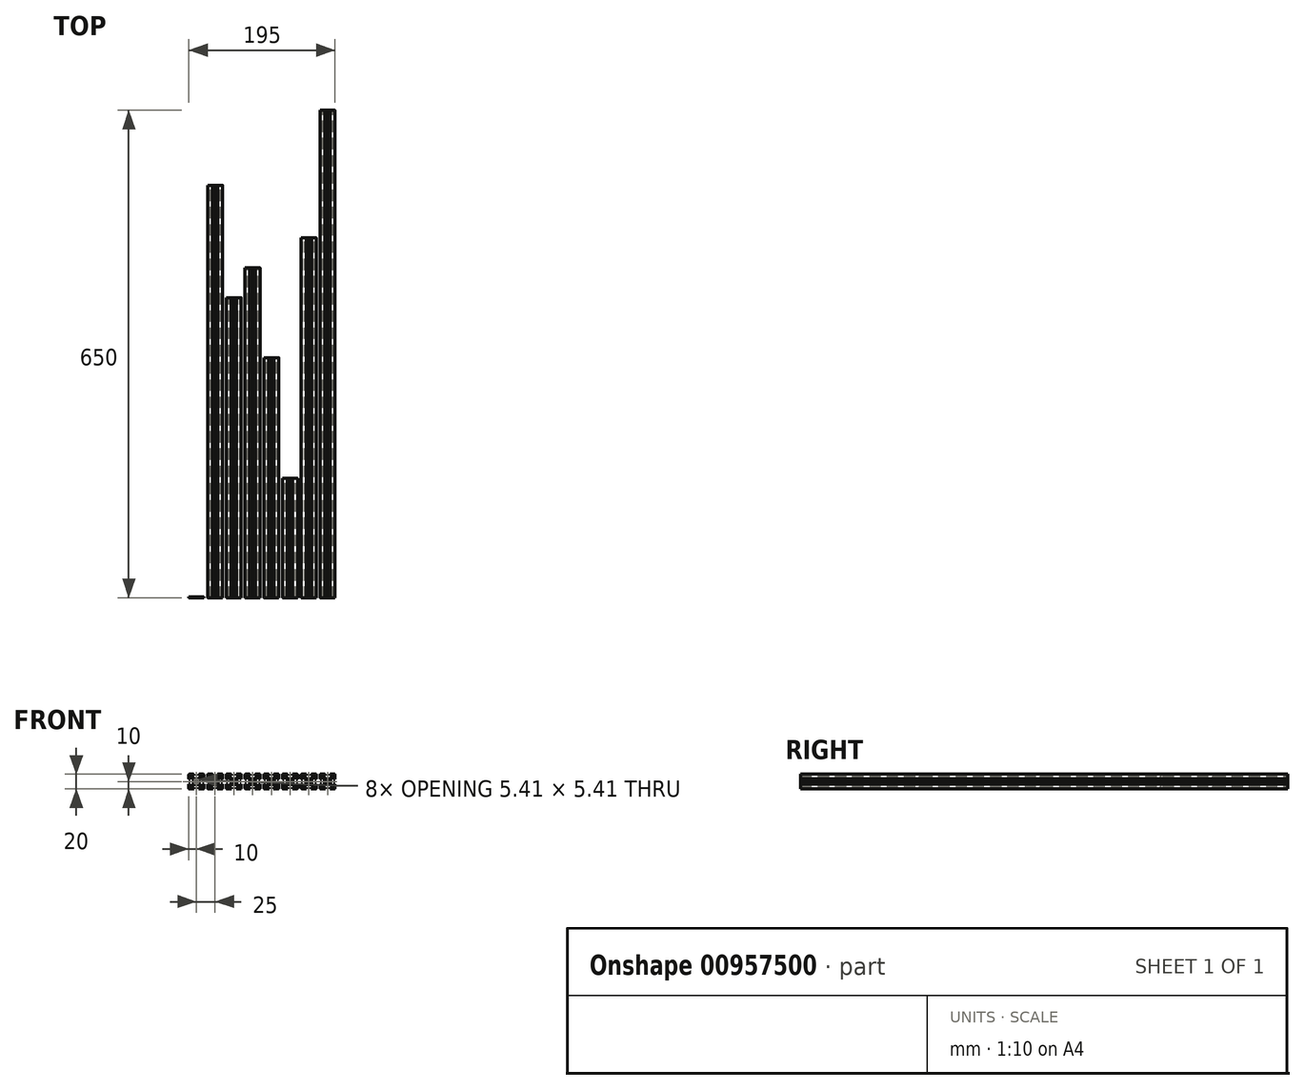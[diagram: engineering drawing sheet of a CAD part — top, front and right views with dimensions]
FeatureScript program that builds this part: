
annotation { "Feature Type Name" : "Feature", "Feature Type Description" : "" }
export const myFeature = defineFeature(function(context is Context, id is Id, definition is map)
    precondition{}
    {
        {
            var Q0;
            Q0=qCreatedBy(makeId("Front.planeOp"),FACE);
            var sketch = newSketch(context, id + "F0", { "sketchPlane" : qUnion([Q0])});
            skArc(sketch, "E0", {"start": v(3.9, -2.93) * mm, "mid": v(3.92, -3.04) * mm, "end": v(3.99, -3.14) * mm});
            skLineSegment(sketch, "E1", {"start": v(3.9, -0.5) * mm, "end": v(3.9, -2.93) * mm});
            skLineSegment(sketch, "E2", {"start": v(3.61, -0.21) * mm, "end": v(3.9, -0.5) * mm});
            skArc(sketch, "E3", {"start": v(3.61, 0.21) * mm, "mid": v(3.52, 0) * mm, "end": v(3.61, -0.21) * mm});
            skLineSegment(sketch, "E4", {"start": v(3.61, 0.21) * mm, "end": v(3.9, 0.5) * mm});
            skLineSegment(sketch, "E5", {"start": v(3.9, 2.93) * mm, "end": v(3.9, 0.5) * mm});
            skArc(sketch, "E6", {"start": v(3.99, 3.14) * mm, "mid": v(3.92, 3.04) * mm, "end": v(3.9, 2.93) * mm});
            skLineSegment(sketch, "E7", {"start": v(3.99, 3.14) * mm, "end": v(6.26, 5.41) * mm});
            skArc(sketch, "E8", {"start": v(6.47, 5.5) * mm, "mid": v(6.36, 5.48) * mm, "end": v(6.26, 5.41) * mm});
            skLineSegment(sketch, "E9", {"start": v(6.47, 5.5) * mm, "end": v(8.1, 5.5) * mm});
            skLineSegment(sketch, "E10", {"start": v(8.1, 3.1) * mm, "end": v(8.1, 5.5) * mm});
            skLineSegment(sketch, "E11", {"start": v(9.5, 3.1) * mm, "end": v(8.1, 3.1) * mm});
            skLineSegment(sketch, "E12", {"start": v(9.5, 3.6) * mm, "end": v(9.5, 3.1) * mm});
            skLineSegment(sketch, "E13", {"start": v(10, 3.6) * mm, "end": v(9.5, 3.6) * mm});
            skLineSegment(sketch, "E14", {"start": v(10, 9) * mm, "end": v(10, 3.6) * mm});
            skArc(sketch, "E15", {"start": v(10, 9) * mm, "mid": v(9.7, 9.7) * mm, "end": v(9, 10) * mm});
            skLineSegment(sketch, "E16", {"start": v(9, 10) * mm, "end": v(3.6, 10) * mm});
            skLineSegment(sketch, "E17", {"start": v(3.6, 9.5) * mm, "end": v(3.6, 10) * mm});
            skLineSegment(sketch, "E18", {"start": v(3.1, 9.5) * mm, "end": v(3.6, 9.5) * mm});
            skLineSegment(sketch, "E19", {"start": v(3.1, 9.5) * mm, "end": v(3.1, 8.1) * mm});
            skLineSegment(sketch, "E20", {"start": v(3.1, 8.1) * mm, "end": v(5.5, 8.1) * mm});
            skLineSegment(sketch, "E21", {"start": v(5.5, 8.1) * mm, "end": v(5.5, 6.47) * mm});
            skArc(sketch, "E22", {"start": v(5.41, 6.26) * mm, "mid": v(5.48, 6.36) * mm, "end": v(5.5, 6.47) * mm});
            skLineSegment(sketch, "E23", {"start": v(3.14, 3.99) * mm, "end": v(5.41, 6.26) * mm});
            skArc(sketch, "E24", {"start": v(2.93, 3.9) * mm, "mid": v(3.04, 3.92) * mm, "end": v(3.14, 3.99) * mm});
            skLineSegment(sketch, "E25", {"start": v(0.5, 3.9) * mm, "end": v(2.93, 3.9) * mm});
            skLineSegment(sketch, "E26", {"start": v(0.21, 3.61) * mm, "end": v(0.5, 3.9) * mm});
            skArc(sketch, "E27", {"start": v(-0.21, 3.61) * mm, "mid": v(0, 3.52) * mm, "end": v(0.21, 3.61) * mm});
            skLineSegment(sketch, "E28", {"start": v(-0.21, 3.61) * mm, "end": v(-0.5, 3.9) * mm});
            skLineSegment(sketch, "E29", {"start": v(-2.93, 3.9) * mm, "end": v(-0.5, 3.9) * mm});
            skArc(sketch, "E30", {"start": v(-3.14, 3.99) * mm, "mid": v(-3.04, 3.92) * mm, "end": v(-2.93, 3.9) * mm});
            skLineSegment(sketch, "E31", {"start": v(-5.41, 6.26) * mm, "end": v(-3.14, 3.99) * mm});
            skArc(sketch, "E32", {"start": v(-5.5, 6.47) * mm, "mid": v(-5.48, 6.36) * mm, "end": v(-5.41, 6.26) * mm});
            skLineSegment(sketch, "E33", {"start": v(-5.5, 6.47) * mm, "end": v(-5.5, 8.1) * mm});
            skLineSegment(sketch, "E34", {"start": v(-3.1, 8.1) * mm, "end": v(-5.5, 8.1) * mm});
            skLineSegment(sketch, "E35", {"start": v(-3.1, 9.5) * mm, "end": v(-3.1, 8.1) * mm});
            skLineSegment(sketch, "E36", {"start": v(-3.1, 9.5) * mm, "end": v(-3.6, 9.5) * mm});
            skLineSegment(sketch, "E37", {"start": v(-3.6, 9.5) * mm, "end": v(-3.6, 10) * mm});
            skLineSegment(sketch, "E38", {"start": v(-9, 10) * mm, "end": v(-3.6, 10) * mm});
            skArc(sketch, "E39", {"start": v(-9, 10) * mm, "mid": v(-9.7, 9.7) * mm, "end": v(-10, 9) * mm});
            skLineSegment(sketch, "E40", {"start": v(-10, 9) * mm, "end": v(-10, 3.6) * mm});
            skLineSegment(sketch, "E41", {"start": v(-10, 3.6) * mm, "end": v(-9.5, 3.6) * mm});
            skLineSegment(sketch, "E42", {"start": v(-9.5, 3.6) * mm, "end": v(-9.5, 3.1) * mm});
            skLineSegment(sketch, "E43", {"start": v(-9.5, 3.1) * mm, "end": v(-8.1, 3.1) * mm});
            skLineSegment(sketch, "E44", {"start": v(-8.1, 3.1) * mm, "end": v(-8.1, 5.5) * mm});
            skLineSegment(sketch, "E45", {"start": v(-8.1, 5.5) * mm, "end": v(-6.47, 5.5) * mm});
            skArc(sketch, "E46", {"start": v(-6.26, 5.41) * mm, "mid": v(-6.36, 5.48) * mm, "end": v(-6.47, 5.5) * mm});
            skLineSegment(sketch, "E47", {"start": v(-3.99, 3.14) * mm, "end": v(-6.26, 5.41) * mm});
            skArc(sketch, "E48", {"start": v(-3.9, 2.93) * mm, "mid": v(-3.92, 3.04) * mm, "end": v(-3.99, 3.14) * mm});
            skLineSegment(sketch, "E49", {"start": v(-3.9, 2.93) * mm, "end": v(-3.9, 0.5) * mm});
            skLineSegment(sketch, "E50", {"start": v(-3.61, 0.21) * mm, "end": v(-3.9, 0.5) * mm});
            skArc(sketch, "E51", {"start": v(-3.61, -0.21) * mm, "mid": v(-3.52, 0) * mm, "end": v(-3.61, 0.21) * mm});
            skLineSegment(sketch, "E52", {"start": v(-3.61, -0.21) * mm, "end": v(-3.9, -0.5) * mm});
            skLineSegment(sketch, "E53", {"start": v(-3.9, -0.5) * mm, "end": v(-3.9, -2.93) * mm});
            skArc(sketch, "E54", {"start": v(-3.99, -3.14) * mm, "mid": v(-3.92, -3.04) * mm, "end": v(-3.9, -2.93) * mm});
            skLineSegment(sketch, "E55", {"start": v(-6.26, -5.41) * mm, "end": v(-3.99, -3.14) * mm});
            skArc(sketch, "E56", {"start": v(-6.47, -5.5) * mm, "mid": v(-6.36, -5.48) * mm, "end": v(-6.26, -5.41) * mm});
            skLineSegment(sketch, "E57", {"start": v(-6.47, -5.5) * mm, "end": v(-8.1, -5.5) * mm});
            skLineSegment(sketch, "E58", {"start": v(-8.1, -3.1) * mm, "end": v(-8.1, -5.5) * mm});
            skLineSegment(sketch, "E59", {"start": v(-9.5, -3.1) * mm, "end": v(-8.1, -3.1) * mm});
            skLineSegment(sketch, "E60", {"start": v(-9.5, -3.6) * mm, "end": v(-9.5, -3.1) * mm});
            skLineSegment(sketch, "E61", {"start": v(-10, -3.6) * mm, "end": v(-9.5, -3.6) * mm});
            skLineSegment(sketch, "E62", {"start": v(-10, -3.6) * mm, "end": v(-10, -9) * mm});
            skArc(sketch, "E63", {"start": v(-10, -9) * mm, "mid": v(-9.7, -9.7) * mm, "end": v(-9, -10) * mm});
            skLineSegment(sketch, "E64", {"start": v(-9, -10) * mm, "end": v(-3.6, -10) * mm});
            skLineSegment(sketch, "E65", {"start": v(-3.6, -9.5) * mm, "end": v(-3.6, -10) * mm});
            skLineSegment(sketch, "E66", {"start": v(-3.1, -9.5) * mm, "end": v(-3.6, -9.5) * mm});
            skLineSegment(sketch, "E67", {"start": v(-3.1, -9.5) * mm, "end": v(-3.1, -8.1) * mm});
            skLineSegment(sketch, "E68", {"start": v(-3.1, -8.1) * mm, "end": v(-5.5, -8.1) * mm});
            skLineSegment(sketch, "E69", {"start": v(-5.5, -8.1) * mm, "end": v(-5.5, -6.47) * mm});
            skArc(sketch, "E70", {"start": v(-5.41, -6.26) * mm, "mid": v(-5.48, -6.36) * mm, "end": v(-5.5, -6.47) * mm});
            skLineSegment(sketch, "E71", {"start": v(-3.14, -3.99) * mm, "end": v(-5.41, -6.26) * mm});
            skArc(sketch, "E72", {"start": v(-2.93, -3.9) * mm, "mid": v(-3.04, -3.92) * mm, "end": v(-3.14, -3.99) * mm});
            skLineSegment(sketch, "E73", {"start": v(-2.93, -3.9) * mm, "end": v(-0.5, -3.9) * mm});
            skLineSegment(sketch, "E74", {"start": v(-0.21, -3.61) * mm, "end": v(-0.5, -3.9) * mm});
            skArc(sketch, "E75", {"start": v(0.21, -3.61) * mm, "mid": v(0, -3.52) * mm, "end": v(-0.21, -3.61) * mm});
            skLineSegment(sketch, "E76", {"start": v(0.21, -3.61) * mm, "end": v(0.5, -3.9) * mm});
            skLineSegment(sketch, "E77", {"start": v(0.5, -3.9) * mm, "end": v(2.93, -3.9) * mm});
            skArc(sketch, "E78", {"start": v(3.14, -3.99) * mm, "mid": v(3.04, -3.92) * mm, "end": v(2.93, -3.9) * mm});
            skLineSegment(sketch, "E79", {"start": v(5.41, -6.26) * mm, "end": v(3.14, -3.99) * mm});
            skArc(sketch, "E80", {"start": v(5.5, -6.47) * mm, "mid": v(5.48, -6.36) * mm, "end": v(5.41, -6.26) * mm});
            skLineSegment(sketch, "E81", {"start": v(5.5, -8.1) * mm, "end": v(5.5, -6.47) * mm});
            skLineSegment(sketch, "E82", {"start": v(3.1, -8.1) * mm, "end": v(5.5, -8.1) * mm});
            skLineSegment(sketch, "E83", {"start": v(3.1, -9.5) * mm, "end": v(3.1, -8.1) * mm});
            skLineSegment(sketch, "E84", {"start": v(3.1, -9.5) * mm, "end": v(3.6, -9.5) * mm});
            skLineSegment(sketch, "E85", {"start": v(3.6, -9.5) * mm, "end": v(3.6, -10) * mm});
            skLineSegment(sketch, "E86", {"start": v(3.6, -10) * mm, "end": v(9, -10) * mm});
            skArc(sketch, "E87", {"start": v(9, -10) * mm, "mid": v(9.7, -9.7) * mm, "end": v(10, -9) * mm});
            skLineSegment(sketch, "E88", {"start": v(10, -3.6) * mm, "end": v(10, -9) * mm});
            skLineSegment(sketch, "E89", {"start": v(10, -3.6) * mm, "end": v(9.5, -3.6) * mm});
            skLineSegment(sketch, "E90", {"start": v(9.5, -3.6) * mm, "end": v(9.5, -3.1) * mm});
            skLineSegment(sketch, "E91", {"start": v(9.5, -3.1) * mm, "end": v(8.1, -3.1) * mm});
            skLineSegment(sketch, "E92", {"start": v(8.1, -3.1) * mm, "end": v(8.1, -5.5) * mm});
            skLineSegment(sketch, "E93", {"start": v(6.47, -5.5) * mm, "end": v(8.1, -5.5) * mm});
            skArc(sketch, "E94", {"start": v(6.26, -5.41) * mm, "mid": v(6.36, -5.48) * mm, "end": v(6.47, -5.5) * mm});
            skLineSegment(sketch, "E95", {"start": v(3.99, -3.14) * mm, "end": v(6.26, -5.41) * mm});
            skLineSegment(sketch, "E96", {"start": v(-1.9, 2.62) * mm, "end": v(-1.54, 2.25) * mm});
            skArc(sketch, "E97", {"start": v(-1.54, 2.25) * mm, "mid": v(-1.37, 2.17) * mm, "end": v(-1.19, 2.2) * mm});
            skArc(sketch, "E98", {"start": v(1.19, 2.2) * mm, "mid": v(0, 2.5) * mm, "end": v(-1.19, 2.2) * mm});
            skArc(sketch, "E99", {"start": v(1.19, 2.2) * mm, "mid": v(1.37, 2.17) * mm, "end": v(1.54, 2.25) * mm});
            skLineSegment(sketch, "E100", {"start": v(1.9, 2.62) * mm, "end": v(1.54, 2.25) * mm});
            skArc(sketch, "E101", {"start": v(2.33, 2.62) * mm, "mid": v(2.12, 2.7) * mm, "end": v(1.9, 2.62) * mm});
            skLineSegment(sketch, "E102", {"start": v(2.62, 2.33) * mm, "end": v(2.33, 2.62) * mm});
            skArc(sketch, "E103", {"start": v(2.62, 1.9) * mm, "mid": v(2.7, 2.12) * mm, "end": v(2.62, 2.33) * mm});
            skLineSegment(sketch, "E104", {"start": v(2.62, 1.9) * mm, "end": v(2.25, 1.54) * mm});
            skArc(sketch, "E105", {"start": v(2.25, 1.54) * mm, "mid": v(2.17, 1.37) * mm, "end": v(2.2, 1.19) * mm});
            skArc(sketch, "E106", {"start": v(2.2, -1.19) * mm, "mid": v(2.5, 0) * mm, "end": v(2.2, 1.19) * mm});
            skArc(sketch, "E107", {"start": v(2.2, -1.19) * mm, "mid": v(2.17, -1.37) * mm, "end": v(2.25, -1.54) * mm});
            skLineSegment(sketch, "E108", {"start": v(2.25, -1.54) * mm, "end": v(2.62, -1.9) * mm});
            skArc(sketch, "E109", {"start": v(2.62, -2.33) * mm, "mid": v(2.7, -2.12) * mm, "end": v(2.62, -1.9) * mm});
            skLineSegment(sketch, "E110", {"start": v(2.33, -2.62) * mm, "end": v(2.62, -2.33) * mm});
            skArc(sketch, "E111", {"start": v(1.9, -2.62) * mm, "mid": v(2.12, -2.7) * mm, "end": v(2.33, -2.62) * mm});
            skLineSegment(sketch, "E112", {"start": v(1.54, -2.25) * mm, "end": v(1.9, -2.62) * mm});
            skArc(sketch, "E113", {"start": v(1.54, -2.25) * mm, "mid": v(1.37, -2.17) * mm, "end": v(1.19, -2.2) * mm});
            skArc(sketch, "E114", {"start": v(-1.19, -2.2) * mm, "mid": v(0, -2.5) * mm, "end": v(1.19, -2.2) * mm});
            skArc(sketch, "E115", {"start": v(-1.19, -2.2) * mm, "mid": v(-1.37, -2.17) * mm, "end": v(-1.54, -2.25) * mm});
            skLineSegment(sketch, "E116", {"start": v(-1.54, -2.25) * mm, "end": v(-1.9, -2.62) * mm});
            skArc(sketch, "E117", {"start": v(-2.33, -2.62) * mm, "mid": v(-2.12, -2.7) * mm, "end": v(-1.9, -2.62) * mm});
            skLineSegment(sketch, "E118", {"start": v(-2.62, -2.33) * mm, "end": v(-2.33, -2.62) * mm});
            skArc(sketch, "E119", {"start": v(-2.62, -1.9) * mm, "mid": v(-2.7, -2.12) * mm, "end": v(-2.62, -2.33) * mm});
            skLineSegment(sketch, "E120", {"start": v(-2.25, -1.54) * mm, "end": v(-2.62, -1.9) * mm});
            skArc(sketch, "E121", {"start": v(-2.25, -1.54) * mm, "mid": v(-2.17, -1.37) * mm, "end": v(-2.2, -1.19) * mm});
            skArc(sketch, "E122", {"start": v(-2.2, 1.19) * mm, "mid": v(-2.5, 0) * mm, "end": v(-2.2, -1.19) * mm});
            skArc(sketch, "E123", {"start": v(-2.2, 1.19) * mm, "mid": v(-2.17, 1.37) * mm, "end": v(-2.25, 1.54) * mm});
            skLineSegment(sketch, "E124", {"start": v(-2.62, 1.9) * mm, "end": v(-2.25, 1.54) * mm});
            skArc(sketch, "E125", {"start": v(-2.62, 2.33) * mm, "mid": v(-2.7, 2.12) * mm, "end": v(-2.62, 1.9) * mm});
            skLineSegment(sketch, "E126", {"start": v(-2.33, 2.62) * mm, "end": v(-2.62, 2.33) * mm});
            skArc(sketch, "E127", {"start": v(-1.9, 2.62) * mm, "mid": v(-2.12, 2.7) * mm, "end": v(-2.33, 2.62) * mm});
            skSolve(sketch);
        }
        {
            var Q0;
            Q0=makeQuery(id+"F0.imprint","IMPRINT",FACE,{"disambiguationData":[TD([[makeQuery(id+"F0.imprint","IMPRINT",EDGE,{"derivedFrom":sQuery(id+"F0.wireOp",EDGE,"E0")}),-1.0]])]});
            extrude(context, id + "F1", {"entities" : qUnion([Q0]), "depth" : 1 * mm, "offsetDistance" : 25 * mm});
        }
        {
            var Q0;
            Q0=makeQuery(id+"F1.opExtrude","SWEPT_BODY",BODY,{"disambiguationData":[OSD([sQuery(id+"F0.wireOp",EDGE,"E0"),sQuery(id+"F0.wireOp",EDGE,"E1"),sQuery(id+"F0.wireOp",EDGE,"E2"),sQuery(id+"F0.wireOp",EDGE,"E3"),sQuery(id+"F0.wireOp",EDGE,"E4"),sQuery(id+"F0.wireOp",EDGE,"E5"),sQuery(id+"F0.wireOp",EDGE,"E6"),sQuery(id+"F0.wireOp",EDGE,"E7"),sQuery(id+"F0.wireOp",EDGE,"E8"),sQuery(id+"F0.wireOp",EDGE,"E9"),sQuery(id+"F0.wireOp",EDGE,"E10"),sQuery(id+"F0.wireOp",EDGE,"E11"),sQuery(id+"F0.wireOp",EDGE,"E12"),sQuery(id+"F0.wireOp",EDGE,"E13"),sQuery(id+"F0.wireOp",EDGE,"E14"),sQuery(id+"F0.wireOp",EDGE,"E15"),sQuery(id+"F0.wireOp",EDGE,"E16"),sQuery(id+"F0.wireOp",EDGE,"E17"),sQuery(id+"F0.wireOp",EDGE,"E18"),sQuery(id+"F0.wireOp",EDGE,"E19"),sQuery(id+"F0.wireOp",EDGE,"E20"),sQuery(id+"F0.wireOp",EDGE,"E21"),sQuery(id+"F0.wireOp",EDGE,"E22"),sQuery(id+"F0.wireOp",EDGE,"E23"),sQuery(id+"F0.wireOp",EDGE,"E24"),sQuery(id+"F0.wireOp",EDGE,"E25"),sQuery(id+"F0.wireOp",EDGE,"E26"),sQuery(id+"F0.wireOp",EDGE,"E27"),sQuery(id+"F0.wireOp",EDGE,"E28"),sQuery(id+"F0.wireOp",EDGE,"E29"),sQuery(id+"F0.wireOp",EDGE,"E30"),sQuery(id+"F0.wireOp",EDGE,"E31"),sQuery(id+"F0.wireOp",EDGE,"E32"),sQuery(id+"F0.wireOp",EDGE,"E33"),sQuery(id+"F0.wireOp",EDGE,"E34"),sQuery(id+"F0.wireOp",EDGE,"E35"),sQuery(id+"F0.wireOp",EDGE,"E36"),sQuery(id+"F0.wireOp",EDGE,"E37"),sQuery(id+"F0.wireOp",EDGE,"E38"),sQuery(id+"F0.wireOp",EDGE,"E39"),sQuery(id+"F0.wireOp",EDGE,"E40"),sQuery(id+"F0.wireOp",EDGE,"E41"),sQuery(id+"F0.wireOp",EDGE,"E42"),sQuery(id+"F0.wireOp",EDGE,"E43"),sQuery(id+"F0.wireOp",EDGE,"E44"),sQuery(id+"F0.wireOp",EDGE,"E45"),sQuery(id+"F0.wireOp",EDGE,"E46"),sQuery(id+"F0.wireOp",EDGE,"E47"),sQuery(id+"F0.wireOp",EDGE,"E48"),sQuery(id+"F0.wireOp",EDGE,"E49"),sQuery(id+"F0.wireOp",EDGE,"E50"),sQuery(id+"F0.wireOp",EDGE,"E51"),sQuery(id+"F0.wireOp",EDGE,"E52"),sQuery(id+"F0.wireOp",EDGE,"E53"),sQuery(id+"F0.wireOp",EDGE,"E54"),sQuery(id+"F0.wireOp",EDGE,"E55"),sQuery(id+"F0.wireOp",EDGE,"E56"),sQuery(id+"F0.wireOp",EDGE,"E57"),sQuery(id+"F0.wireOp",EDGE,"E58"),sQuery(id+"F0.wireOp",EDGE,"E59"),sQuery(id+"F0.wireOp",EDGE,"E60"),sQuery(id+"F0.wireOp",EDGE,"E61"),sQuery(id+"F0.wireOp",EDGE,"E62"),sQuery(id+"F0.wireOp",EDGE,"E63"),sQuery(id+"F0.wireOp",EDGE,"E64"),sQuery(id+"F0.wireOp",EDGE,"E65"),sQuery(id+"F0.wireOp",EDGE,"E66"),sQuery(id+"F0.wireOp",EDGE,"E67"),sQuery(id+"F0.wireOp",EDGE,"E68"),sQuery(id+"F0.wireOp",EDGE,"E69"),sQuery(id+"F0.wireOp",EDGE,"E70"),sQuery(id+"F0.wireOp",EDGE,"E71"),sQuery(id+"F0.wireOp",EDGE,"E72"),sQuery(id+"F0.wireOp",EDGE,"E73"),sQuery(id+"F0.wireOp",EDGE,"E74"),sQuery(id+"F0.wireOp",EDGE,"E75"),sQuery(id+"F0.wireOp",EDGE,"E76"),sQuery(id+"F0.wireOp",EDGE,"E77"),sQuery(id+"F0.wireOp",EDGE,"E78"),sQuery(id+"F0.wireOp",EDGE,"E79"),sQuery(id+"F0.wireOp",EDGE,"E80"),sQuery(id+"F0.wireOp",EDGE,"E81"),sQuery(id+"F0.wireOp",EDGE,"E82"),sQuery(id+"F0.wireOp",EDGE,"E83"),sQuery(id+"F0.wireOp",EDGE,"E84"),sQuery(id+"F0.wireOp",EDGE,"E85"),sQuery(id+"F0.wireOp",EDGE,"E86"),sQuery(id+"F0.wireOp",EDGE,"E87"),sQuery(id+"F0.wireOp",EDGE,"E88"),sQuery(id+"F0.wireOp",EDGE,"E89"),sQuery(id+"F0.wireOp",EDGE,"E90"),sQuery(id+"F0.wireOp",EDGE,"E91"),sQuery(id+"F0.wireOp",EDGE,"E92"),sQuery(id+"F0.wireOp",EDGE,"E93"),sQuery(id+"F0.wireOp",EDGE,"E94"),sQuery(id+"F0.wireOp",EDGE,"E95"),sQuery(id+"F0.wireOp",EDGE,"E96"),sQuery(id+"F0.wireOp",EDGE,"E97"),sQuery(id+"F0.wireOp",EDGE,"E98"),sQuery(id+"F0.wireOp",EDGE,"E99"),sQuery(id+"F0.wireOp",EDGE,"E100"),sQuery(id+"F0.wireOp",EDGE,"E101"),sQuery(id+"F0.wireOp",EDGE,"E102"),sQuery(id+"F0.wireOp",EDGE,"E103"),sQuery(id+"F0.wireOp",EDGE,"E104"),sQuery(id+"F0.wireOp",EDGE,"E105"),sQuery(id+"F0.wireOp",EDGE,"E106"),sQuery(id+"F0.wireOp",EDGE,"E107"),sQuery(id+"F0.wireOp",EDGE,"E108"),sQuery(id+"F0.wireOp",EDGE,"E109"),sQuery(id+"F0.wireOp",EDGE,"E110"),sQuery(id+"F0.wireOp",EDGE,"E111"),sQuery(id+"F0.wireOp",EDGE,"E112"),sQuery(id+"F0.wireOp",EDGE,"E113"),sQuery(id+"F0.wireOp",EDGE,"E114"),sQuery(id+"F0.wireOp",EDGE,"E115"),sQuery(id+"F0.wireOp",EDGE,"E116"),sQuery(id+"F0.wireOp",EDGE,"E117"),sQuery(id+"F0.wireOp",EDGE,"E118"),sQuery(id+"F0.wireOp",EDGE,"E119"),sQuery(id+"F0.wireOp",EDGE,"E120"),sQuery(id+"F0.wireOp",EDGE,"E121"),sQuery(id+"F0.wireOp",EDGE,"E122"),sQuery(id+"F0.wireOp",EDGE,"E123"),sQuery(id+"F0.wireOp",EDGE,"E124"),sQuery(id+"F0.wireOp",EDGE,"E125"),sQuery(id+"F0.wireOp",EDGE,"E126"),sQuery(id+"F0.wireOp",EDGE,"E127")])]});
            transform(context, id + "F2", {"entities" : qUnion([Q0]), "transformType" : TransformType.TRANSLATION_3D, "dx" : 25 * mm, "dy" : 0 * mm, "dz" : 0 * mm, "makeCopy" : true});
        }
        {
            var Q0;
            Q0=makeQuery(id+"F2.opPattern","COPY",FACE,{"derivedFrom":makeQuery(id+"F1.opExtrude","CAP_FACE",FACE,{"disambiguationData":[OSD([sQuery(id+"F0.wireOp",EDGE,"E0"),sQuery(id+"F0.wireOp",EDGE,"E1"),sQuery(id+"F0.wireOp",EDGE,"E2"),sQuery(id+"F0.wireOp",EDGE,"E3"),sQuery(id+"F0.wireOp",EDGE,"E4"),sQuery(id+"F0.wireOp",EDGE,"E5"),sQuery(id+"F0.wireOp",EDGE,"E6"),sQuery(id+"F0.wireOp",EDGE,"E7"),sQuery(id+"F0.wireOp",EDGE,"E8"),sQuery(id+"F0.wireOp",EDGE,"E9"),sQuery(id+"F0.wireOp",EDGE,"E10"),sQuery(id+"F0.wireOp",EDGE,"E11"),sQuery(id+"F0.wireOp",EDGE,"E12"),sQuery(id+"F0.wireOp",EDGE,"E13"),sQuery(id+"F0.wireOp",EDGE,"E14"),sQuery(id+"F0.wireOp",EDGE,"E15"),sQuery(id+"F0.wireOp",EDGE,"E16"),sQuery(id+"F0.wireOp",EDGE,"E17"),sQuery(id+"F0.wireOp",EDGE,"E18"),sQuery(id+"F0.wireOp",EDGE,"E19"),sQuery(id+"F0.wireOp",EDGE,"E20"),sQuery(id+"F0.wireOp",EDGE,"E21"),sQuery(id+"F0.wireOp",EDGE,"E22"),sQuery(id+"F0.wireOp",EDGE,"E23"),sQuery(id+"F0.wireOp",EDGE,"E24"),sQuery(id+"F0.wireOp",EDGE,"E25"),sQuery(id+"F0.wireOp",EDGE,"E26"),sQuery(id+"F0.wireOp",EDGE,"E27"),sQuery(id+"F0.wireOp",EDGE,"E28"),sQuery(id+"F0.wireOp",EDGE,"E29"),sQuery(id+"F0.wireOp",EDGE,"E30"),sQuery(id+"F0.wireOp",EDGE,"E31"),sQuery(id+"F0.wireOp",EDGE,"E32"),sQuery(id+"F0.wireOp",EDGE,"E33"),sQuery(id+"F0.wireOp",EDGE,"E34"),sQuery(id+"F0.wireOp",EDGE,"E35"),sQuery(id+"F0.wireOp",EDGE,"E36"),sQuery(id+"F0.wireOp",EDGE,"E37"),sQuery(id+"F0.wireOp",EDGE,"E38"),sQuery(id+"F0.wireOp",EDGE,"E39"),sQuery(id+"F0.wireOp",EDGE,"E40"),sQuery(id+"F0.wireOp",EDGE,"E41"),sQuery(id+"F0.wireOp",EDGE,"E42"),sQuery(id+"F0.wireOp",EDGE,"E43"),sQuery(id+"F0.wireOp",EDGE,"E44"),sQuery(id+"F0.wireOp",EDGE,"E45"),sQuery(id+"F0.wireOp",EDGE,"E46"),sQuery(id+"F0.wireOp",EDGE,"E47"),sQuery(id+"F0.wireOp",EDGE,"E48"),sQuery(id+"F0.wireOp",EDGE,"E49"),sQuery(id+"F0.wireOp",EDGE,"E50"),sQuery(id+"F0.wireOp",EDGE,"E51"),sQuery(id+"F0.wireOp",EDGE,"E52"),sQuery(id+"F0.wireOp",EDGE,"E53"),sQuery(id+"F0.wireOp",EDGE,"E54"),sQuery(id+"F0.wireOp",EDGE,"E55"),sQuery(id+"F0.wireOp",EDGE,"E56"),sQuery(id+"F0.wireOp",EDGE,"E57"),sQuery(id+"F0.wireOp",EDGE,"E58"),sQuery(id+"F0.wireOp",EDGE,"E59"),sQuery(id+"F0.wireOp",EDGE,"E60"),sQuery(id+"F0.wireOp",EDGE,"E61"),sQuery(id+"F0.wireOp",EDGE,"E62"),sQuery(id+"F0.wireOp",EDGE,"E63"),sQuery(id+"F0.wireOp",EDGE,"E64"),sQuery(id+"F0.wireOp",EDGE,"E65"),sQuery(id+"F0.wireOp",EDGE,"E66"),sQuery(id+"F0.wireOp",EDGE,"E67"),sQuery(id+"F0.wireOp",EDGE,"E68"),sQuery(id+"F0.wireOp",EDGE,"E69"),sQuery(id+"F0.wireOp",EDGE,"E70"),sQuery(id+"F0.wireOp",EDGE,"E71"),sQuery(id+"F0.wireOp",EDGE,"E72"),sQuery(id+"F0.wireOp",EDGE,"E73"),sQuery(id+"F0.wireOp",EDGE,"E74"),sQuery(id+"F0.wireOp",EDGE,"E75"),sQuery(id+"F0.wireOp",EDGE,"E76"),sQuery(id+"F0.wireOp",EDGE,"E77"),sQuery(id+"F0.wireOp",EDGE,"E78"),sQuery(id+"F0.wireOp",EDGE,"E79"),sQuery(id+"F0.wireOp",EDGE,"E80"),sQuery(id+"F0.wireOp",EDGE,"E81"),sQuery(id+"F0.wireOp",EDGE,"E82"),sQuery(id+"F0.wireOp",EDGE,"E83"),sQuery(id+"F0.wireOp",EDGE,"E84"),sQuery(id+"F0.wireOp",EDGE,"E85"),sQuery(id+"F0.wireOp",EDGE,"E86"),sQuery(id+"F0.wireOp",EDGE,"E87"),sQuery(id+"F0.wireOp",EDGE,"E88"),sQuery(id+"F0.wireOp",EDGE,"E89"),sQuery(id+"F0.wireOp",EDGE,"E90"),sQuery(id+"F0.wireOp",EDGE,"E91"),sQuery(id+"F0.wireOp",EDGE,"E92"),sQuery(id+"F0.wireOp",EDGE,"E93"),sQuery(id+"F0.wireOp",EDGE,"E94"),sQuery(id+"F0.wireOp",EDGE,"E95"),sQuery(id+"F0.wireOp",EDGE,"E96"),sQuery(id+"F0.wireOp",EDGE,"E97"),sQuery(id+"F0.wireOp",EDGE,"E98"),sQuery(id+"F0.wireOp",EDGE,"E99"),sQuery(id+"F0.wireOp",EDGE,"E100"),sQuery(id+"F0.wireOp",EDGE,"E101"),sQuery(id+"F0.wireOp",EDGE,"E102"),sQuery(id+"F0.wireOp",EDGE,"E103"),sQuery(id+"F0.wireOp",EDGE,"E104"),sQuery(id+"F0.wireOp",EDGE,"E105"),sQuery(id+"F0.wireOp",EDGE,"E106"),sQuery(id+"F0.wireOp",EDGE,"E107"),sQuery(id+"F0.wireOp",EDGE,"E108"),sQuery(id+"F0.wireOp",EDGE,"E109"),sQuery(id+"F0.wireOp",EDGE,"E110"),sQuery(id+"F0.wireOp",EDGE,"E111"),sQuery(id+"F0.wireOp",EDGE,"E112"),sQuery(id+"F0.wireOp",EDGE,"E113"),sQuery(id+"F0.wireOp",EDGE,"E114"),sQuery(id+"F0.wireOp",EDGE,"E115"),sQuery(id+"F0.wireOp",EDGE,"E116"),sQuery(id+"F0.wireOp",EDGE,"E117"),sQuery(id+"F0.wireOp",EDGE,"E118"),sQuery(id+"F0.wireOp",EDGE,"E119"),sQuery(id+"F0.wireOp",EDGE,"E120"),sQuery(id+"F0.wireOp",EDGE,"E121"),sQuery(id+"F0.wireOp",EDGE,"E122"),sQuery(id+"F0.wireOp",EDGE,"E123"),sQuery(id+"F0.wireOp",EDGE,"E124"),sQuery(id+"F0.wireOp",EDGE,"E125"),sQuery(id+"F0.wireOp",EDGE,"E126"),sQuery(id+"F0.wireOp",EDGE,"E127")])],"isStart":true}),"instanceName":"1"});
            extrude(context, id + "F3", {"entities" : qUnion([Q0]), "operationType" : NewBodyOperationType.ADD, "depth" : (550 - 1) * mm, "offsetDistance" : 25 * mm});
        }
        {
            var Q0;
            Q0=makeQuery(id+"F1.opExtrude","SWEPT_BODY",BODY,{"disambiguationData":[OSD([sQuery(id+"F0.wireOp",EDGE,"E0"),sQuery(id+"F0.wireOp",EDGE,"E1"),sQuery(id+"F0.wireOp",EDGE,"E2"),sQuery(id+"F0.wireOp",EDGE,"E3"),sQuery(id+"F0.wireOp",EDGE,"E4"),sQuery(id+"F0.wireOp",EDGE,"E5"),sQuery(id+"F0.wireOp",EDGE,"E6"),sQuery(id+"F0.wireOp",EDGE,"E7"),sQuery(id+"F0.wireOp",EDGE,"E8"),sQuery(id+"F0.wireOp",EDGE,"E9"),sQuery(id+"F0.wireOp",EDGE,"E10"),sQuery(id+"F0.wireOp",EDGE,"E11"),sQuery(id+"F0.wireOp",EDGE,"E12"),sQuery(id+"F0.wireOp",EDGE,"E13"),sQuery(id+"F0.wireOp",EDGE,"E14"),sQuery(id+"F0.wireOp",EDGE,"E15"),sQuery(id+"F0.wireOp",EDGE,"E16"),sQuery(id+"F0.wireOp",EDGE,"E17"),sQuery(id+"F0.wireOp",EDGE,"E18"),sQuery(id+"F0.wireOp",EDGE,"E19"),sQuery(id+"F0.wireOp",EDGE,"E20"),sQuery(id+"F0.wireOp",EDGE,"E21"),sQuery(id+"F0.wireOp",EDGE,"E22"),sQuery(id+"F0.wireOp",EDGE,"E23"),sQuery(id+"F0.wireOp",EDGE,"E24"),sQuery(id+"F0.wireOp",EDGE,"E25"),sQuery(id+"F0.wireOp",EDGE,"E26"),sQuery(id+"F0.wireOp",EDGE,"E27"),sQuery(id+"F0.wireOp",EDGE,"E28"),sQuery(id+"F0.wireOp",EDGE,"E29"),sQuery(id+"F0.wireOp",EDGE,"E30"),sQuery(id+"F0.wireOp",EDGE,"E31"),sQuery(id+"F0.wireOp",EDGE,"E32"),sQuery(id+"F0.wireOp",EDGE,"E33"),sQuery(id+"F0.wireOp",EDGE,"E34"),sQuery(id+"F0.wireOp",EDGE,"E35"),sQuery(id+"F0.wireOp",EDGE,"E36"),sQuery(id+"F0.wireOp",EDGE,"E37"),sQuery(id+"F0.wireOp",EDGE,"E38"),sQuery(id+"F0.wireOp",EDGE,"E39"),sQuery(id+"F0.wireOp",EDGE,"E40"),sQuery(id+"F0.wireOp",EDGE,"E41"),sQuery(id+"F0.wireOp",EDGE,"E42"),sQuery(id+"F0.wireOp",EDGE,"E43"),sQuery(id+"F0.wireOp",EDGE,"E44"),sQuery(id+"F0.wireOp",EDGE,"E45"),sQuery(id+"F0.wireOp",EDGE,"E46"),sQuery(id+"F0.wireOp",EDGE,"E47"),sQuery(id+"F0.wireOp",EDGE,"E48"),sQuery(id+"F0.wireOp",EDGE,"E49"),sQuery(id+"F0.wireOp",EDGE,"E50"),sQuery(id+"F0.wireOp",EDGE,"E51"),sQuery(id+"F0.wireOp",EDGE,"E52"),sQuery(id+"F0.wireOp",EDGE,"E53"),sQuery(id+"F0.wireOp",EDGE,"E54"),sQuery(id+"F0.wireOp",EDGE,"E55"),sQuery(id+"F0.wireOp",EDGE,"E56"),sQuery(id+"F0.wireOp",EDGE,"E57"),sQuery(id+"F0.wireOp",EDGE,"E58"),sQuery(id+"F0.wireOp",EDGE,"E59"),sQuery(id+"F0.wireOp",EDGE,"E60"),sQuery(id+"F0.wireOp",EDGE,"E61"),sQuery(id+"F0.wireOp",EDGE,"E62"),sQuery(id+"F0.wireOp",EDGE,"E63"),sQuery(id+"F0.wireOp",EDGE,"E64"),sQuery(id+"F0.wireOp",EDGE,"E65"),sQuery(id+"F0.wireOp",EDGE,"E66"),sQuery(id+"F0.wireOp",EDGE,"E67"),sQuery(id+"F0.wireOp",EDGE,"E68"),sQuery(id+"F0.wireOp",EDGE,"E69"),sQuery(id+"F0.wireOp",EDGE,"E70"),sQuery(id+"F0.wireOp",EDGE,"E71"),sQuery(id+"F0.wireOp",EDGE,"E72"),sQuery(id+"F0.wireOp",EDGE,"E73"),sQuery(id+"F0.wireOp",EDGE,"E74"),sQuery(id+"F0.wireOp",EDGE,"E75"),sQuery(id+"F0.wireOp",EDGE,"E76"),sQuery(id+"F0.wireOp",EDGE,"E77"),sQuery(id+"F0.wireOp",EDGE,"E78"),sQuery(id+"F0.wireOp",EDGE,"E79"),sQuery(id+"F0.wireOp",EDGE,"E80"),sQuery(id+"F0.wireOp",EDGE,"E81"),sQuery(id+"F0.wireOp",EDGE,"E82"),sQuery(id+"F0.wireOp",EDGE,"E83"),sQuery(id+"F0.wireOp",EDGE,"E84"),sQuery(id+"F0.wireOp",EDGE,"E85"),sQuery(id+"F0.wireOp",EDGE,"E86"),sQuery(id+"F0.wireOp",EDGE,"E87"),sQuery(id+"F0.wireOp",EDGE,"E88"),sQuery(id+"F0.wireOp",EDGE,"E89"),sQuery(id+"F0.wireOp",EDGE,"E90"),sQuery(id+"F0.wireOp",EDGE,"E91"),sQuery(id+"F0.wireOp",EDGE,"E92"),sQuery(id+"F0.wireOp",EDGE,"E93"),sQuery(id+"F0.wireOp",EDGE,"E94"),sQuery(id+"F0.wireOp",EDGE,"E95"),sQuery(id+"F0.wireOp",EDGE,"E96"),sQuery(id+"F0.wireOp",EDGE,"E97"),sQuery(id+"F0.wireOp",EDGE,"E98"),sQuery(id+"F0.wireOp",EDGE,"E99"),sQuery(id+"F0.wireOp",EDGE,"E100"),sQuery(id+"F0.wireOp",EDGE,"E101"),sQuery(id+"F0.wireOp",EDGE,"E102"),sQuery(id+"F0.wireOp",EDGE,"E103"),sQuery(id+"F0.wireOp",EDGE,"E104"),sQuery(id+"F0.wireOp",EDGE,"E105"),sQuery(id+"F0.wireOp",EDGE,"E106"),sQuery(id+"F0.wireOp",EDGE,"E107"),sQuery(id+"F0.wireOp",EDGE,"E108"),sQuery(id+"F0.wireOp",EDGE,"E109"),sQuery(id+"F0.wireOp",EDGE,"E110"),sQuery(id+"F0.wireOp",EDGE,"E111"),sQuery(id+"F0.wireOp",EDGE,"E112"),sQuery(id+"F0.wireOp",EDGE,"E113"),sQuery(id+"F0.wireOp",EDGE,"E114"),sQuery(id+"F0.wireOp",EDGE,"E115"),sQuery(id+"F0.wireOp",EDGE,"E116"),sQuery(id+"F0.wireOp",EDGE,"E117"),sQuery(id+"F0.wireOp",EDGE,"E118"),sQuery(id+"F0.wireOp",EDGE,"E119"),sQuery(id+"F0.wireOp",EDGE,"E120"),sQuery(id+"F0.wireOp",EDGE,"E121"),sQuery(id+"F0.wireOp",EDGE,"E122"),sQuery(id+"F0.wireOp",EDGE,"E123"),sQuery(id+"F0.wireOp",EDGE,"E124"),sQuery(id+"F0.wireOp",EDGE,"E125"),sQuery(id+"F0.wireOp",EDGE,"E126"),sQuery(id+"F0.wireOp",EDGE,"E127")])]});
            transform(context, id + "F4", {"entities" : qUnion([Q0]), "transformType" : TransformType.TRANSLATION_3D, "dx" : (25 * 2) * mm, "dy" : 0 * mm, "dz" : 0 * mm, "makeCopy" : true});
        }
        {
            var Q0;
            Q0=makeQuery(id+"F4.opPattern","COPY",FACE,{"derivedFrom":makeQuery(id+"F1.opExtrude","CAP_FACE",FACE,{"disambiguationData":[OSD([sQuery(id+"F0.wireOp",EDGE,"E0"),sQuery(id+"F0.wireOp",EDGE,"E1"),sQuery(id+"F0.wireOp",EDGE,"E2"),sQuery(id+"F0.wireOp",EDGE,"E3"),sQuery(id+"F0.wireOp",EDGE,"E4"),sQuery(id+"F0.wireOp",EDGE,"E5"),sQuery(id+"F0.wireOp",EDGE,"E6"),sQuery(id+"F0.wireOp",EDGE,"E7"),sQuery(id+"F0.wireOp",EDGE,"E8"),sQuery(id+"F0.wireOp",EDGE,"E9"),sQuery(id+"F0.wireOp",EDGE,"E10"),sQuery(id+"F0.wireOp",EDGE,"E11"),sQuery(id+"F0.wireOp",EDGE,"E12"),sQuery(id+"F0.wireOp",EDGE,"E13"),sQuery(id+"F0.wireOp",EDGE,"E14"),sQuery(id+"F0.wireOp",EDGE,"E15"),sQuery(id+"F0.wireOp",EDGE,"E16"),sQuery(id+"F0.wireOp",EDGE,"E17"),sQuery(id+"F0.wireOp",EDGE,"E18"),sQuery(id+"F0.wireOp",EDGE,"E19"),sQuery(id+"F0.wireOp",EDGE,"E20"),sQuery(id+"F0.wireOp",EDGE,"E21"),sQuery(id+"F0.wireOp",EDGE,"E22"),sQuery(id+"F0.wireOp",EDGE,"E23"),sQuery(id+"F0.wireOp",EDGE,"E24"),sQuery(id+"F0.wireOp",EDGE,"E25"),sQuery(id+"F0.wireOp",EDGE,"E26"),sQuery(id+"F0.wireOp",EDGE,"E27"),sQuery(id+"F0.wireOp",EDGE,"E28"),sQuery(id+"F0.wireOp",EDGE,"E29"),sQuery(id+"F0.wireOp",EDGE,"E30"),sQuery(id+"F0.wireOp",EDGE,"E31"),sQuery(id+"F0.wireOp",EDGE,"E32"),sQuery(id+"F0.wireOp",EDGE,"E33"),sQuery(id+"F0.wireOp",EDGE,"E34"),sQuery(id+"F0.wireOp",EDGE,"E35"),sQuery(id+"F0.wireOp",EDGE,"E36"),sQuery(id+"F0.wireOp",EDGE,"E37"),sQuery(id+"F0.wireOp",EDGE,"E38"),sQuery(id+"F0.wireOp",EDGE,"E39"),sQuery(id+"F0.wireOp",EDGE,"E40"),sQuery(id+"F0.wireOp",EDGE,"E41"),sQuery(id+"F0.wireOp",EDGE,"E42"),sQuery(id+"F0.wireOp",EDGE,"E43"),sQuery(id+"F0.wireOp",EDGE,"E44"),sQuery(id+"F0.wireOp",EDGE,"E45"),sQuery(id+"F0.wireOp",EDGE,"E46"),sQuery(id+"F0.wireOp",EDGE,"E47"),sQuery(id+"F0.wireOp",EDGE,"E48"),sQuery(id+"F0.wireOp",EDGE,"E49"),sQuery(id+"F0.wireOp",EDGE,"E50"),sQuery(id+"F0.wireOp",EDGE,"E51"),sQuery(id+"F0.wireOp",EDGE,"E52"),sQuery(id+"F0.wireOp",EDGE,"E53"),sQuery(id+"F0.wireOp",EDGE,"E54"),sQuery(id+"F0.wireOp",EDGE,"E55"),sQuery(id+"F0.wireOp",EDGE,"E56"),sQuery(id+"F0.wireOp",EDGE,"E57"),sQuery(id+"F0.wireOp",EDGE,"E58"),sQuery(id+"F0.wireOp",EDGE,"E59"),sQuery(id+"F0.wireOp",EDGE,"E60"),sQuery(id+"F0.wireOp",EDGE,"E61"),sQuery(id+"F0.wireOp",EDGE,"E62"),sQuery(id+"F0.wireOp",EDGE,"E63"),sQuery(id+"F0.wireOp",EDGE,"E64"),sQuery(id+"F0.wireOp",EDGE,"E65"),sQuery(id+"F0.wireOp",EDGE,"E66"),sQuery(id+"F0.wireOp",EDGE,"E67"),sQuery(id+"F0.wireOp",EDGE,"E68"),sQuery(id+"F0.wireOp",EDGE,"E69"),sQuery(id+"F0.wireOp",EDGE,"E70"),sQuery(id+"F0.wireOp",EDGE,"E71"),sQuery(id+"F0.wireOp",EDGE,"E72"),sQuery(id+"F0.wireOp",EDGE,"E73"),sQuery(id+"F0.wireOp",EDGE,"E74"),sQuery(id+"F0.wireOp",EDGE,"E75"),sQuery(id+"F0.wireOp",EDGE,"E76"),sQuery(id+"F0.wireOp",EDGE,"E77"),sQuery(id+"F0.wireOp",EDGE,"E78"),sQuery(id+"F0.wireOp",EDGE,"E79"),sQuery(id+"F0.wireOp",EDGE,"E80"),sQuery(id+"F0.wireOp",EDGE,"E81"),sQuery(id+"F0.wireOp",EDGE,"E82"),sQuery(id+"F0.wireOp",EDGE,"E83"),sQuery(id+"F0.wireOp",EDGE,"E84"),sQuery(id+"F0.wireOp",EDGE,"E85"),sQuery(id+"F0.wireOp",EDGE,"E86"),sQuery(id+"F0.wireOp",EDGE,"E87"),sQuery(id+"F0.wireOp",EDGE,"E88"),sQuery(id+"F0.wireOp",EDGE,"E89"),sQuery(id+"F0.wireOp",EDGE,"E90"),sQuery(id+"F0.wireOp",EDGE,"E91"),sQuery(id+"F0.wireOp",EDGE,"E92"),sQuery(id+"F0.wireOp",EDGE,"E93"),sQuery(id+"F0.wireOp",EDGE,"E94"),sQuery(id+"F0.wireOp",EDGE,"E95"),sQuery(id+"F0.wireOp",EDGE,"E96"),sQuery(id+"F0.wireOp",EDGE,"E97"),sQuery(id+"F0.wireOp",EDGE,"E98"),sQuery(id+"F0.wireOp",EDGE,"E99"),sQuery(id+"F0.wireOp",EDGE,"E100"),sQuery(id+"F0.wireOp",EDGE,"E101"),sQuery(id+"F0.wireOp",EDGE,"E102"),sQuery(id+"F0.wireOp",EDGE,"E103"),sQuery(id+"F0.wireOp",EDGE,"E104"),sQuery(id+"F0.wireOp",EDGE,"E105"),sQuery(id+"F0.wireOp",EDGE,"E106"),sQuery(id+"F0.wireOp",EDGE,"E107"),sQuery(id+"F0.wireOp",EDGE,"E108"),sQuery(id+"F0.wireOp",EDGE,"E109"),sQuery(id+"F0.wireOp",EDGE,"E110"),sQuery(id+"F0.wireOp",EDGE,"E111"),sQuery(id+"F0.wireOp",EDGE,"E112"),sQuery(id+"F0.wireOp",EDGE,"E113"),sQuery(id+"F0.wireOp",EDGE,"E114"),sQuery(id+"F0.wireOp",EDGE,"E115"),sQuery(id+"F0.wireOp",EDGE,"E116"),sQuery(id+"F0.wireOp",EDGE,"E117"),sQuery(id+"F0.wireOp",EDGE,"E118"),sQuery(id+"F0.wireOp",EDGE,"E119"),sQuery(id+"F0.wireOp",EDGE,"E120"),sQuery(id+"F0.wireOp",EDGE,"E121"),sQuery(id+"F0.wireOp",EDGE,"E122"),sQuery(id+"F0.wireOp",EDGE,"E123"),sQuery(id+"F0.wireOp",EDGE,"E124"),sQuery(id+"F0.wireOp",EDGE,"E125"),sQuery(id+"F0.wireOp",EDGE,"E126"),sQuery(id+"F0.wireOp",EDGE,"E127")])],"isStart":true}),"instanceName":"1"});
            extrude(context, id + "F5", {"entities" : qUnion([Q0]), "operationType" : NewBodyOperationType.ADD, "depth" : (400 - 1) * mm, "offsetDistance" : 25 * mm});
        }
        {
            var Q0;
            Q0=makeQuery(id+"F1.opExtrude","SWEPT_BODY",BODY,{"disambiguationData":[OSD([sQuery(id+"F0.wireOp",EDGE,"E0"),sQuery(id+"F0.wireOp",EDGE,"E1"),sQuery(id+"F0.wireOp",EDGE,"E2"),sQuery(id+"F0.wireOp",EDGE,"E3"),sQuery(id+"F0.wireOp",EDGE,"E4"),sQuery(id+"F0.wireOp",EDGE,"E5"),sQuery(id+"F0.wireOp",EDGE,"E6"),sQuery(id+"F0.wireOp",EDGE,"E7"),sQuery(id+"F0.wireOp",EDGE,"E8"),sQuery(id+"F0.wireOp",EDGE,"E9"),sQuery(id+"F0.wireOp",EDGE,"E10"),sQuery(id+"F0.wireOp",EDGE,"E11"),sQuery(id+"F0.wireOp",EDGE,"E12"),sQuery(id+"F0.wireOp",EDGE,"E13"),sQuery(id+"F0.wireOp",EDGE,"E14"),sQuery(id+"F0.wireOp",EDGE,"E15"),sQuery(id+"F0.wireOp",EDGE,"E16"),sQuery(id+"F0.wireOp",EDGE,"E17"),sQuery(id+"F0.wireOp",EDGE,"E18"),sQuery(id+"F0.wireOp",EDGE,"E19"),sQuery(id+"F0.wireOp",EDGE,"E20"),sQuery(id+"F0.wireOp",EDGE,"E21"),sQuery(id+"F0.wireOp",EDGE,"E22"),sQuery(id+"F0.wireOp",EDGE,"E23"),sQuery(id+"F0.wireOp",EDGE,"E24"),sQuery(id+"F0.wireOp",EDGE,"E25"),sQuery(id+"F0.wireOp",EDGE,"E26"),sQuery(id+"F0.wireOp",EDGE,"E27"),sQuery(id+"F0.wireOp",EDGE,"E28"),sQuery(id+"F0.wireOp",EDGE,"E29"),sQuery(id+"F0.wireOp",EDGE,"E30"),sQuery(id+"F0.wireOp",EDGE,"E31"),sQuery(id+"F0.wireOp",EDGE,"E32"),sQuery(id+"F0.wireOp",EDGE,"E33"),sQuery(id+"F0.wireOp",EDGE,"E34"),sQuery(id+"F0.wireOp",EDGE,"E35"),sQuery(id+"F0.wireOp",EDGE,"E36"),sQuery(id+"F0.wireOp",EDGE,"E37"),sQuery(id+"F0.wireOp",EDGE,"E38"),sQuery(id+"F0.wireOp",EDGE,"E39"),sQuery(id+"F0.wireOp",EDGE,"E40"),sQuery(id+"F0.wireOp",EDGE,"E41"),sQuery(id+"F0.wireOp",EDGE,"E42"),sQuery(id+"F0.wireOp",EDGE,"E43"),sQuery(id+"F0.wireOp",EDGE,"E44"),sQuery(id+"F0.wireOp",EDGE,"E45"),sQuery(id+"F0.wireOp",EDGE,"E46"),sQuery(id+"F0.wireOp",EDGE,"E47"),sQuery(id+"F0.wireOp",EDGE,"E48"),sQuery(id+"F0.wireOp",EDGE,"E49"),sQuery(id+"F0.wireOp",EDGE,"E50"),sQuery(id+"F0.wireOp",EDGE,"E51"),sQuery(id+"F0.wireOp",EDGE,"E52"),sQuery(id+"F0.wireOp",EDGE,"E53"),sQuery(id+"F0.wireOp",EDGE,"E54"),sQuery(id+"F0.wireOp",EDGE,"E55"),sQuery(id+"F0.wireOp",EDGE,"E56"),sQuery(id+"F0.wireOp",EDGE,"E57"),sQuery(id+"F0.wireOp",EDGE,"E58"),sQuery(id+"F0.wireOp",EDGE,"E59"),sQuery(id+"F0.wireOp",EDGE,"E60"),sQuery(id+"F0.wireOp",EDGE,"E61"),sQuery(id+"F0.wireOp",EDGE,"E62"),sQuery(id+"F0.wireOp",EDGE,"E63"),sQuery(id+"F0.wireOp",EDGE,"E64"),sQuery(id+"F0.wireOp",EDGE,"E65"),sQuery(id+"F0.wireOp",EDGE,"E66"),sQuery(id+"F0.wireOp",EDGE,"E67"),sQuery(id+"F0.wireOp",EDGE,"E68"),sQuery(id+"F0.wireOp",EDGE,"E69"),sQuery(id+"F0.wireOp",EDGE,"E70"),sQuery(id+"F0.wireOp",EDGE,"E71"),sQuery(id+"F0.wireOp",EDGE,"E72"),sQuery(id+"F0.wireOp",EDGE,"E73"),sQuery(id+"F0.wireOp",EDGE,"E74"),sQuery(id+"F0.wireOp",EDGE,"E75"),sQuery(id+"F0.wireOp",EDGE,"E76"),sQuery(id+"F0.wireOp",EDGE,"E77"),sQuery(id+"F0.wireOp",EDGE,"E78"),sQuery(id+"F0.wireOp",EDGE,"E79"),sQuery(id+"F0.wireOp",EDGE,"E80"),sQuery(id+"F0.wireOp",EDGE,"E81"),sQuery(id+"F0.wireOp",EDGE,"E82"),sQuery(id+"F0.wireOp",EDGE,"E83"),sQuery(id+"F0.wireOp",EDGE,"E84"),sQuery(id+"F0.wireOp",EDGE,"E85"),sQuery(id+"F0.wireOp",EDGE,"E86"),sQuery(id+"F0.wireOp",EDGE,"E87"),sQuery(id+"F0.wireOp",EDGE,"E88"),sQuery(id+"F0.wireOp",EDGE,"E89"),sQuery(id+"F0.wireOp",EDGE,"E90"),sQuery(id+"F0.wireOp",EDGE,"E91"),sQuery(id+"F0.wireOp",EDGE,"E92"),sQuery(id+"F0.wireOp",EDGE,"E93"),sQuery(id+"F0.wireOp",EDGE,"E94"),sQuery(id+"F0.wireOp",EDGE,"E95"),sQuery(id+"F0.wireOp",EDGE,"E96"),sQuery(id+"F0.wireOp",EDGE,"E97"),sQuery(id+"F0.wireOp",EDGE,"E98"),sQuery(id+"F0.wireOp",EDGE,"E99"),sQuery(id+"F0.wireOp",EDGE,"E100"),sQuery(id+"F0.wireOp",EDGE,"E101"),sQuery(id+"F0.wireOp",EDGE,"E102"),sQuery(id+"F0.wireOp",EDGE,"E103"),sQuery(id+"F0.wireOp",EDGE,"E104"),sQuery(id+"F0.wireOp",EDGE,"E105"),sQuery(id+"F0.wireOp",EDGE,"E106"),sQuery(id+"F0.wireOp",EDGE,"E107"),sQuery(id+"F0.wireOp",EDGE,"E108"),sQuery(id+"F0.wireOp",EDGE,"E109"),sQuery(id+"F0.wireOp",EDGE,"E110"),sQuery(id+"F0.wireOp",EDGE,"E111"),sQuery(id+"F0.wireOp",EDGE,"E112"),sQuery(id+"F0.wireOp",EDGE,"E113"),sQuery(id+"F0.wireOp",EDGE,"E114"),sQuery(id+"F0.wireOp",EDGE,"E115"),sQuery(id+"F0.wireOp",EDGE,"E116"),sQuery(id+"F0.wireOp",EDGE,"E117"),sQuery(id+"F0.wireOp",EDGE,"E118"),sQuery(id+"F0.wireOp",EDGE,"E119"),sQuery(id+"F0.wireOp",EDGE,"E120"),sQuery(id+"F0.wireOp",EDGE,"E121"),sQuery(id+"F0.wireOp",EDGE,"E122"),sQuery(id+"F0.wireOp",EDGE,"E123"),sQuery(id+"F0.wireOp",EDGE,"E124"),sQuery(id+"F0.wireOp",EDGE,"E125"),sQuery(id+"F0.wireOp",EDGE,"E126"),sQuery(id+"F0.wireOp",EDGE,"E127")])]});
            transform(context, id + "F6", {"entities" : qUnion([Q0]), "transformType" : TransformType.TRANSLATION_3D, "dx" : (25 * 3) * mm, "dy" : 0 * mm, "dz" : 0 * mm, "makeCopy" : true});
        }
        {
            var Q0;
            Q0=makeQuery(id+"F1.opExtrude","SWEPT_BODY",BODY,{"disambiguationData":[OSD([sQuery(id+"F0.wireOp",EDGE,"E0"),sQuery(id+"F0.wireOp",EDGE,"E1"),sQuery(id+"F0.wireOp",EDGE,"E2"),sQuery(id+"F0.wireOp",EDGE,"E3"),sQuery(id+"F0.wireOp",EDGE,"E4"),sQuery(id+"F0.wireOp",EDGE,"E5"),sQuery(id+"F0.wireOp",EDGE,"E6"),sQuery(id+"F0.wireOp",EDGE,"E7"),sQuery(id+"F0.wireOp",EDGE,"E8"),sQuery(id+"F0.wireOp",EDGE,"E9"),sQuery(id+"F0.wireOp",EDGE,"E10"),sQuery(id+"F0.wireOp",EDGE,"E11"),sQuery(id+"F0.wireOp",EDGE,"E12"),sQuery(id+"F0.wireOp",EDGE,"E13"),sQuery(id+"F0.wireOp",EDGE,"E14"),sQuery(id+"F0.wireOp",EDGE,"E15"),sQuery(id+"F0.wireOp",EDGE,"E16"),sQuery(id+"F0.wireOp",EDGE,"E17"),sQuery(id+"F0.wireOp",EDGE,"E18"),sQuery(id+"F0.wireOp",EDGE,"E19"),sQuery(id+"F0.wireOp",EDGE,"E20"),sQuery(id+"F0.wireOp",EDGE,"E21"),sQuery(id+"F0.wireOp",EDGE,"E22"),sQuery(id+"F0.wireOp",EDGE,"E23"),sQuery(id+"F0.wireOp",EDGE,"E24"),sQuery(id+"F0.wireOp",EDGE,"E25"),sQuery(id+"F0.wireOp",EDGE,"E26"),sQuery(id+"F0.wireOp",EDGE,"E27"),sQuery(id+"F0.wireOp",EDGE,"E28"),sQuery(id+"F0.wireOp",EDGE,"E29"),sQuery(id+"F0.wireOp",EDGE,"E30"),sQuery(id+"F0.wireOp",EDGE,"E31"),sQuery(id+"F0.wireOp",EDGE,"E32"),sQuery(id+"F0.wireOp",EDGE,"E33"),sQuery(id+"F0.wireOp",EDGE,"E34"),sQuery(id+"F0.wireOp",EDGE,"E35"),sQuery(id+"F0.wireOp",EDGE,"E36"),sQuery(id+"F0.wireOp",EDGE,"E37"),sQuery(id+"F0.wireOp",EDGE,"E38"),sQuery(id+"F0.wireOp",EDGE,"E39"),sQuery(id+"F0.wireOp",EDGE,"E40"),sQuery(id+"F0.wireOp",EDGE,"E41"),sQuery(id+"F0.wireOp",EDGE,"E42"),sQuery(id+"F0.wireOp",EDGE,"E43"),sQuery(id+"F0.wireOp",EDGE,"E44"),sQuery(id+"F0.wireOp",EDGE,"E45"),sQuery(id+"F0.wireOp",EDGE,"E46"),sQuery(id+"F0.wireOp",EDGE,"E47"),sQuery(id+"F0.wireOp",EDGE,"E48"),sQuery(id+"F0.wireOp",EDGE,"E49"),sQuery(id+"F0.wireOp",EDGE,"E50"),sQuery(id+"F0.wireOp",EDGE,"E51"),sQuery(id+"F0.wireOp",EDGE,"E52"),sQuery(id+"F0.wireOp",EDGE,"E53"),sQuery(id+"F0.wireOp",EDGE,"E54"),sQuery(id+"F0.wireOp",EDGE,"E55"),sQuery(id+"F0.wireOp",EDGE,"E56"),sQuery(id+"F0.wireOp",EDGE,"E57"),sQuery(id+"F0.wireOp",EDGE,"E58"),sQuery(id+"F0.wireOp",EDGE,"E59"),sQuery(id+"F0.wireOp",EDGE,"E60"),sQuery(id+"F0.wireOp",EDGE,"E61"),sQuery(id+"F0.wireOp",EDGE,"E62"),sQuery(id+"F0.wireOp",EDGE,"E63"),sQuery(id+"F0.wireOp",EDGE,"E64"),sQuery(id+"F0.wireOp",EDGE,"E65"),sQuery(id+"F0.wireOp",EDGE,"E66"),sQuery(id+"F0.wireOp",EDGE,"E67"),sQuery(id+"F0.wireOp",EDGE,"E68"),sQuery(id+"F0.wireOp",EDGE,"E69"),sQuery(id+"F0.wireOp",EDGE,"E70"),sQuery(id+"F0.wireOp",EDGE,"E71"),sQuery(id+"F0.wireOp",EDGE,"E72"),sQuery(id+"F0.wireOp",EDGE,"E73"),sQuery(id+"F0.wireOp",EDGE,"E74"),sQuery(id+"F0.wireOp",EDGE,"E75"),sQuery(id+"F0.wireOp",EDGE,"E76"),sQuery(id+"F0.wireOp",EDGE,"E77"),sQuery(id+"F0.wireOp",EDGE,"E78"),sQuery(id+"F0.wireOp",EDGE,"E79"),sQuery(id+"F0.wireOp",EDGE,"E80"),sQuery(id+"F0.wireOp",EDGE,"E81"),sQuery(id+"F0.wireOp",EDGE,"E82"),sQuery(id+"F0.wireOp",EDGE,"E83"),sQuery(id+"F0.wireOp",EDGE,"E84"),sQuery(id+"F0.wireOp",EDGE,"E85"),sQuery(id+"F0.wireOp",EDGE,"E86"),sQuery(id+"F0.wireOp",EDGE,"E87"),sQuery(id+"F0.wireOp",EDGE,"E88"),sQuery(id+"F0.wireOp",EDGE,"E89"),sQuery(id+"F0.wireOp",EDGE,"E90"),sQuery(id+"F0.wireOp",EDGE,"E91"),sQuery(id+"F0.wireOp",EDGE,"E92"),sQuery(id+"F0.wireOp",EDGE,"E93"),sQuery(id+"F0.wireOp",EDGE,"E94"),sQuery(id+"F0.wireOp",EDGE,"E95"),sQuery(id+"F0.wireOp",EDGE,"E96"),sQuery(id+"F0.wireOp",EDGE,"E97"),sQuery(id+"F0.wireOp",EDGE,"E98"),sQuery(id+"F0.wireOp",EDGE,"E99"),sQuery(id+"F0.wireOp",EDGE,"E100"),sQuery(id+"F0.wireOp",EDGE,"E101"),sQuery(id+"F0.wireOp",EDGE,"E102"),sQuery(id+"F0.wireOp",EDGE,"E103"),sQuery(id+"F0.wireOp",EDGE,"E104"),sQuery(id+"F0.wireOp",EDGE,"E105"),sQuery(id+"F0.wireOp",EDGE,"E106"),sQuery(id+"F0.wireOp",EDGE,"E107"),sQuery(id+"F0.wireOp",EDGE,"E108"),sQuery(id+"F0.wireOp",EDGE,"E109"),sQuery(id+"F0.wireOp",EDGE,"E110"),sQuery(id+"F0.wireOp",EDGE,"E111"),sQuery(id+"F0.wireOp",EDGE,"E112"),sQuery(id+"F0.wireOp",EDGE,"E113"),sQuery(id+"F0.wireOp",EDGE,"E114"),sQuery(id+"F0.wireOp",EDGE,"E115"),sQuery(id+"F0.wireOp",EDGE,"E116"),sQuery(id+"F0.wireOp",EDGE,"E117"),sQuery(id+"F0.wireOp",EDGE,"E118"),sQuery(id+"F0.wireOp",EDGE,"E119"),sQuery(id+"F0.wireOp",EDGE,"E120"),sQuery(id+"F0.wireOp",EDGE,"E121"),sQuery(id+"F0.wireOp",EDGE,"E122"),sQuery(id+"F0.wireOp",EDGE,"E123"),sQuery(id+"F0.wireOp",EDGE,"E124"),sQuery(id+"F0.wireOp",EDGE,"E125"),sQuery(id+"F0.wireOp",EDGE,"E126"),sQuery(id+"F0.wireOp",EDGE,"E127")])]});
            transform(context, id + "F7", {"entities" : qUnion([Q0]), "transformType" : TransformType.TRANSLATION_3D, "dx" : (25 * 4) * mm, "dy" : 0 * mm, "dz" : 0 * mm, "makeCopy" : true});
        }
        {
            var Q0;
            Q0=makeQuery(id+"F1.opExtrude","SWEPT_BODY",BODY,{"disambiguationData":[OSD([sQuery(id+"F0.wireOp",EDGE,"E0"),sQuery(id+"F0.wireOp",EDGE,"E1"),sQuery(id+"F0.wireOp",EDGE,"E2"),sQuery(id+"F0.wireOp",EDGE,"E3"),sQuery(id+"F0.wireOp",EDGE,"E4"),sQuery(id+"F0.wireOp",EDGE,"E5"),sQuery(id+"F0.wireOp",EDGE,"E6"),sQuery(id+"F0.wireOp",EDGE,"E7"),sQuery(id+"F0.wireOp",EDGE,"E8"),sQuery(id+"F0.wireOp",EDGE,"E9"),sQuery(id+"F0.wireOp",EDGE,"E10"),sQuery(id+"F0.wireOp",EDGE,"E11"),sQuery(id+"F0.wireOp",EDGE,"E12"),sQuery(id+"F0.wireOp",EDGE,"E13"),sQuery(id+"F0.wireOp",EDGE,"E14"),sQuery(id+"F0.wireOp",EDGE,"E15"),sQuery(id+"F0.wireOp",EDGE,"E16"),sQuery(id+"F0.wireOp",EDGE,"E17"),sQuery(id+"F0.wireOp",EDGE,"E18"),sQuery(id+"F0.wireOp",EDGE,"E19"),sQuery(id+"F0.wireOp",EDGE,"E20"),sQuery(id+"F0.wireOp",EDGE,"E21"),sQuery(id+"F0.wireOp",EDGE,"E22"),sQuery(id+"F0.wireOp",EDGE,"E23"),sQuery(id+"F0.wireOp",EDGE,"E24"),sQuery(id+"F0.wireOp",EDGE,"E25"),sQuery(id+"F0.wireOp",EDGE,"E26"),sQuery(id+"F0.wireOp",EDGE,"E27"),sQuery(id+"F0.wireOp",EDGE,"E28"),sQuery(id+"F0.wireOp",EDGE,"E29"),sQuery(id+"F0.wireOp",EDGE,"E30"),sQuery(id+"F0.wireOp",EDGE,"E31"),sQuery(id+"F0.wireOp",EDGE,"E32"),sQuery(id+"F0.wireOp",EDGE,"E33"),sQuery(id+"F0.wireOp",EDGE,"E34"),sQuery(id+"F0.wireOp",EDGE,"E35"),sQuery(id+"F0.wireOp",EDGE,"E36"),sQuery(id+"F0.wireOp",EDGE,"E37"),sQuery(id+"F0.wireOp",EDGE,"E38"),sQuery(id+"F0.wireOp",EDGE,"E39"),sQuery(id+"F0.wireOp",EDGE,"E40"),sQuery(id+"F0.wireOp",EDGE,"E41"),sQuery(id+"F0.wireOp",EDGE,"E42"),sQuery(id+"F0.wireOp",EDGE,"E43"),sQuery(id+"F0.wireOp",EDGE,"E44"),sQuery(id+"F0.wireOp",EDGE,"E45"),sQuery(id+"F0.wireOp",EDGE,"E46"),sQuery(id+"F0.wireOp",EDGE,"E47"),sQuery(id+"F0.wireOp",EDGE,"E48"),sQuery(id+"F0.wireOp",EDGE,"E49"),sQuery(id+"F0.wireOp",EDGE,"E50"),sQuery(id+"F0.wireOp",EDGE,"E51"),sQuery(id+"F0.wireOp",EDGE,"E52"),sQuery(id+"F0.wireOp",EDGE,"E53"),sQuery(id+"F0.wireOp",EDGE,"E54"),sQuery(id+"F0.wireOp",EDGE,"E55"),sQuery(id+"F0.wireOp",EDGE,"E56"),sQuery(id+"F0.wireOp",EDGE,"E57"),sQuery(id+"F0.wireOp",EDGE,"E58"),sQuery(id+"F0.wireOp",EDGE,"E59"),sQuery(id+"F0.wireOp",EDGE,"E60"),sQuery(id+"F0.wireOp",EDGE,"E61"),sQuery(id+"F0.wireOp",EDGE,"E62"),sQuery(id+"F0.wireOp",EDGE,"E63"),sQuery(id+"F0.wireOp",EDGE,"E64"),sQuery(id+"F0.wireOp",EDGE,"E65"),sQuery(id+"F0.wireOp",EDGE,"E66"),sQuery(id+"F0.wireOp",EDGE,"E67"),sQuery(id+"F0.wireOp",EDGE,"E68"),sQuery(id+"F0.wireOp",EDGE,"E69"),sQuery(id+"F0.wireOp",EDGE,"E70"),sQuery(id+"F0.wireOp",EDGE,"E71"),sQuery(id+"F0.wireOp",EDGE,"E72"),sQuery(id+"F0.wireOp",EDGE,"E73"),sQuery(id+"F0.wireOp",EDGE,"E74"),sQuery(id+"F0.wireOp",EDGE,"E75"),sQuery(id+"F0.wireOp",EDGE,"E76"),sQuery(id+"F0.wireOp",EDGE,"E77"),sQuery(id+"F0.wireOp",EDGE,"E78"),sQuery(id+"F0.wireOp",EDGE,"E79"),sQuery(id+"F0.wireOp",EDGE,"E80"),sQuery(id+"F0.wireOp",EDGE,"E81"),sQuery(id+"F0.wireOp",EDGE,"E82"),sQuery(id+"F0.wireOp",EDGE,"E83"),sQuery(id+"F0.wireOp",EDGE,"E84"),sQuery(id+"F0.wireOp",EDGE,"E85"),sQuery(id+"F0.wireOp",EDGE,"E86"),sQuery(id+"F0.wireOp",EDGE,"E87"),sQuery(id+"F0.wireOp",EDGE,"E88"),sQuery(id+"F0.wireOp",EDGE,"E89"),sQuery(id+"F0.wireOp",EDGE,"E90"),sQuery(id+"F0.wireOp",EDGE,"E91"),sQuery(id+"F0.wireOp",EDGE,"E92"),sQuery(id+"F0.wireOp",EDGE,"E93"),sQuery(id+"F0.wireOp",EDGE,"E94"),sQuery(id+"F0.wireOp",EDGE,"E95"),sQuery(id+"F0.wireOp",EDGE,"E96"),sQuery(id+"F0.wireOp",EDGE,"E97"),sQuery(id+"F0.wireOp",EDGE,"E98"),sQuery(id+"F0.wireOp",EDGE,"E99"),sQuery(id+"F0.wireOp",EDGE,"E100"),sQuery(id+"F0.wireOp",EDGE,"E101"),sQuery(id+"F0.wireOp",EDGE,"E102"),sQuery(id+"F0.wireOp",EDGE,"E103"),sQuery(id+"F0.wireOp",EDGE,"E104"),sQuery(id+"F0.wireOp",EDGE,"E105"),sQuery(id+"F0.wireOp",EDGE,"E106"),sQuery(id+"F0.wireOp",EDGE,"E107"),sQuery(id+"F0.wireOp",EDGE,"E108"),sQuery(id+"F0.wireOp",EDGE,"E109"),sQuery(id+"F0.wireOp",EDGE,"E110"),sQuery(id+"F0.wireOp",EDGE,"E111"),sQuery(id+"F0.wireOp",EDGE,"E112"),sQuery(id+"F0.wireOp",EDGE,"E113"),sQuery(id+"F0.wireOp",EDGE,"E114"),sQuery(id+"F0.wireOp",EDGE,"E115"),sQuery(id+"F0.wireOp",EDGE,"E116"),sQuery(id+"F0.wireOp",EDGE,"E117"),sQuery(id+"F0.wireOp",EDGE,"E118"),sQuery(id+"F0.wireOp",EDGE,"E119"),sQuery(id+"F0.wireOp",EDGE,"E120"),sQuery(id+"F0.wireOp",EDGE,"E121"),sQuery(id+"F0.wireOp",EDGE,"E122"),sQuery(id+"F0.wireOp",EDGE,"E123"),sQuery(id+"F0.wireOp",EDGE,"E124"),sQuery(id+"F0.wireOp",EDGE,"E125"),sQuery(id+"F0.wireOp",EDGE,"E126"),sQuery(id+"F0.wireOp",EDGE,"E127")])]});
            transform(context, id + "F8", {"entities" : qUnion([Q0]), "transformType" : TransformType.TRANSLATION_3D, "dx" : (25 * 5) * mm, "dy" : 0 * mm, "dz" : 0 * mm, "makeCopy" : true});
        }
        {
            var Q0;
            Q0=makeQuery(id+"F6.opPattern","COPY",FACE,{"derivedFrom":makeQuery(id+"F1.opExtrude","CAP_FACE",FACE,{"disambiguationData":[OSD([sQuery(id+"F0.wireOp",EDGE,"E0"),sQuery(id+"F0.wireOp",EDGE,"E1"),sQuery(id+"F0.wireOp",EDGE,"E2"),sQuery(id+"F0.wireOp",EDGE,"E3"),sQuery(id+"F0.wireOp",EDGE,"E4"),sQuery(id+"F0.wireOp",EDGE,"E5"),sQuery(id+"F0.wireOp",EDGE,"E6"),sQuery(id+"F0.wireOp",EDGE,"E7"),sQuery(id+"F0.wireOp",EDGE,"E8"),sQuery(id+"F0.wireOp",EDGE,"E9"),sQuery(id+"F0.wireOp",EDGE,"E10"),sQuery(id+"F0.wireOp",EDGE,"E11"),sQuery(id+"F0.wireOp",EDGE,"E12"),sQuery(id+"F0.wireOp",EDGE,"E13"),sQuery(id+"F0.wireOp",EDGE,"E14"),sQuery(id+"F0.wireOp",EDGE,"E15"),sQuery(id+"F0.wireOp",EDGE,"E16"),sQuery(id+"F0.wireOp",EDGE,"E17"),sQuery(id+"F0.wireOp",EDGE,"E18"),sQuery(id+"F0.wireOp",EDGE,"E19"),sQuery(id+"F0.wireOp",EDGE,"E20"),sQuery(id+"F0.wireOp",EDGE,"E21"),sQuery(id+"F0.wireOp",EDGE,"E22"),sQuery(id+"F0.wireOp",EDGE,"E23"),sQuery(id+"F0.wireOp",EDGE,"E24"),sQuery(id+"F0.wireOp",EDGE,"E25"),sQuery(id+"F0.wireOp",EDGE,"E26"),sQuery(id+"F0.wireOp",EDGE,"E27"),sQuery(id+"F0.wireOp",EDGE,"E28"),sQuery(id+"F0.wireOp",EDGE,"E29"),sQuery(id+"F0.wireOp",EDGE,"E30"),sQuery(id+"F0.wireOp",EDGE,"E31"),sQuery(id+"F0.wireOp",EDGE,"E32"),sQuery(id+"F0.wireOp",EDGE,"E33"),sQuery(id+"F0.wireOp",EDGE,"E34"),sQuery(id+"F0.wireOp",EDGE,"E35"),sQuery(id+"F0.wireOp",EDGE,"E36"),sQuery(id+"F0.wireOp",EDGE,"E37"),sQuery(id+"F0.wireOp",EDGE,"E38"),sQuery(id+"F0.wireOp",EDGE,"E39"),sQuery(id+"F0.wireOp",EDGE,"E40"),sQuery(id+"F0.wireOp",EDGE,"E41"),sQuery(id+"F0.wireOp",EDGE,"E42"),sQuery(id+"F0.wireOp",EDGE,"E43"),sQuery(id+"F0.wireOp",EDGE,"E44"),sQuery(id+"F0.wireOp",EDGE,"E45"),sQuery(id+"F0.wireOp",EDGE,"E46"),sQuery(id+"F0.wireOp",EDGE,"E47"),sQuery(id+"F0.wireOp",EDGE,"E48"),sQuery(id+"F0.wireOp",EDGE,"E49"),sQuery(id+"F0.wireOp",EDGE,"E50"),sQuery(id+"F0.wireOp",EDGE,"E51"),sQuery(id+"F0.wireOp",EDGE,"E52"),sQuery(id+"F0.wireOp",EDGE,"E53"),sQuery(id+"F0.wireOp",EDGE,"E54"),sQuery(id+"F0.wireOp",EDGE,"E55"),sQuery(id+"F0.wireOp",EDGE,"E56"),sQuery(id+"F0.wireOp",EDGE,"E57"),sQuery(id+"F0.wireOp",EDGE,"E58"),sQuery(id+"F0.wireOp",EDGE,"E59"),sQuery(id+"F0.wireOp",EDGE,"E60"),sQuery(id+"F0.wireOp",EDGE,"E61"),sQuery(id+"F0.wireOp",EDGE,"E62"),sQuery(id+"F0.wireOp",EDGE,"E63"),sQuery(id+"F0.wireOp",EDGE,"E64"),sQuery(id+"F0.wireOp",EDGE,"E65"),sQuery(id+"F0.wireOp",EDGE,"E66"),sQuery(id+"F0.wireOp",EDGE,"E67"),sQuery(id+"F0.wireOp",EDGE,"E68"),sQuery(id+"F0.wireOp",EDGE,"E69"),sQuery(id+"F0.wireOp",EDGE,"E70"),sQuery(id+"F0.wireOp",EDGE,"E71"),sQuery(id+"F0.wireOp",EDGE,"E72"),sQuery(id+"F0.wireOp",EDGE,"E73"),sQuery(id+"F0.wireOp",EDGE,"E74"),sQuery(id+"F0.wireOp",EDGE,"E75"),sQuery(id+"F0.wireOp",EDGE,"E76"),sQuery(id+"F0.wireOp",EDGE,"E77"),sQuery(id+"F0.wireOp",EDGE,"E78"),sQuery(id+"F0.wireOp",EDGE,"E79"),sQuery(id+"F0.wireOp",EDGE,"E80"),sQuery(id+"F0.wireOp",EDGE,"E81"),sQuery(id+"F0.wireOp",EDGE,"E82"),sQuery(id+"F0.wireOp",EDGE,"E83"),sQuery(id+"F0.wireOp",EDGE,"E84"),sQuery(id+"F0.wireOp",EDGE,"E85"),sQuery(id+"F0.wireOp",EDGE,"E86"),sQuery(id+"F0.wireOp",EDGE,"E87"),sQuery(id+"F0.wireOp",EDGE,"E88"),sQuery(id+"F0.wireOp",EDGE,"E89"),sQuery(id+"F0.wireOp",EDGE,"E90"),sQuery(id+"F0.wireOp",EDGE,"E91"),sQuery(id+"F0.wireOp",EDGE,"E92"),sQuery(id+"F0.wireOp",EDGE,"E93"),sQuery(id+"F0.wireOp",EDGE,"E94"),sQuery(id+"F0.wireOp",EDGE,"E95"),sQuery(id+"F0.wireOp",EDGE,"E96"),sQuery(id+"F0.wireOp",EDGE,"E97"),sQuery(id+"F0.wireOp",EDGE,"E98"),sQuery(id+"F0.wireOp",EDGE,"E99"),sQuery(id+"F0.wireOp",EDGE,"E100"),sQuery(id+"F0.wireOp",EDGE,"E101"),sQuery(id+"F0.wireOp",EDGE,"E102"),sQuery(id+"F0.wireOp",EDGE,"E103"),sQuery(id+"F0.wireOp",EDGE,"E104"),sQuery(id+"F0.wireOp",EDGE,"E105"),sQuery(id+"F0.wireOp",EDGE,"E106"),sQuery(id+"F0.wireOp",EDGE,"E107"),sQuery(id+"F0.wireOp",EDGE,"E108"),sQuery(id+"F0.wireOp",EDGE,"E109"),sQuery(id+"F0.wireOp",EDGE,"E110"),sQuery(id+"F0.wireOp",EDGE,"E111"),sQuery(id+"F0.wireOp",EDGE,"E112"),sQuery(id+"F0.wireOp",EDGE,"E113"),sQuery(id+"F0.wireOp",EDGE,"E114"),sQuery(id+"F0.wireOp",EDGE,"E115"),sQuery(id+"F0.wireOp",EDGE,"E116"),sQuery(id+"F0.wireOp",EDGE,"E117"),sQuery(id+"F0.wireOp",EDGE,"E118"),sQuery(id+"F0.wireOp",EDGE,"E119"),sQuery(id+"F0.wireOp",EDGE,"E120"),sQuery(id+"F0.wireOp",EDGE,"E121"),sQuery(id+"F0.wireOp",EDGE,"E122"),sQuery(id+"F0.wireOp",EDGE,"E123"),sQuery(id+"F0.wireOp",EDGE,"E124"),sQuery(id+"F0.wireOp",EDGE,"E125"),sQuery(id+"F0.wireOp",EDGE,"E126"),sQuery(id+"F0.wireOp",EDGE,"E127")])],"isStart":true}),"instanceName":"1"});
            extrude(context, id + "F9", {"entities" : qUnion([Q0]), "operationType" : NewBodyOperationType.ADD, "depth" : (440 - 1) * mm, "offsetDistance" : 25 * mm});
        }
        {
            var Q0;
            Q0=makeQuery(id+"F7.opPattern","COPY",FACE,{"derivedFrom":makeQuery(id+"F1.opExtrude","CAP_FACE",FACE,{"disambiguationData":[OSD([sQuery(id+"F0.wireOp",EDGE,"E0"),sQuery(id+"F0.wireOp",EDGE,"E1"),sQuery(id+"F0.wireOp",EDGE,"E2"),sQuery(id+"F0.wireOp",EDGE,"E3"),sQuery(id+"F0.wireOp",EDGE,"E4"),sQuery(id+"F0.wireOp",EDGE,"E5"),sQuery(id+"F0.wireOp",EDGE,"E6"),sQuery(id+"F0.wireOp",EDGE,"E7"),sQuery(id+"F0.wireOp",EDGE,"E8"),sQuery(id+"F0.wireOp",EDGE,"E9"),sQuery(id+"F0.wireOp",EDGE,"E10"),sQuery(id+"F0.wireOp",EDGE,"E11"),sQuery(id+"F0.wireOp",EDGE,"E12"),sQuery(id+"F0.wireOp",EDGE,"E13"),sQuery(id+"F0.wireOp",EDGE,"E14"),sQuery(id+"F0.wireOp",EDGE,"E15"),sQuery(id+"F0.wireOp",EDGE,"E16"),sQuery(id+"F0.wireOp",EDGE,"E17"),sQuery(id+"F0.wireOp",EDGE,"E18"),sQuery(id+"F0.wireOp",EDGE,"E19"),sQuery(id+"F0.wireOp",EDGE,"E20"),sQuery(id+"F0.wireOp",EDGE,"E21"),sQuery(id+"F0.wireOp",EDGE,"E22"),sQuery(id+"F0.wireOp",EDGE,"E23"),sQuery(id+"F0.wireOp",EDGE,"E24"),sQuery(id+"F0.wireOp",EDGE,"E25"),sQuery(id+"F0.wireOp",EDGE,"E26"),sQuery(id+"F0.wireOp",EDGE,"E27"),sQuery(id+"F0.wireOp",EDGE,"E28"),sQuery(id+"F0.wireOp",EDGE,"E29"),sQuery(id+"F0.wireOp",EDGE,"E30"),sQuery(id+"F0.wireOp",EDGE,"E31"),sQuery(id+"F0.wireOp",EDGE,"E32"),sQuery(id+"F0.wireOp",EDGE,"E33"),sQuery(id+"F0.wireOp",EDGE,"E34"),sQuery(id+"F0.wireOp",EDGE,"E35"),sQuery(id+"F0.wireOp",EDGE,"E36"),sQuery(id+"F0.wireOp",EDGE,"E37"),sQuery(id+"F0.wireOp",EDGE,"E38"),sQuery(id+"F0.wireOp",EDGE,"E39"),sQuery(id+"F0.wireOp",EDGE,"E40"),sQuery(id+"F0.wireOp",EDGE,"E41"),sQuery(id+"F0.wireOp",EDGE,"E42"),sQuery(id+"F0.wireOp",EDGE,"E43"),sQuery(id+"F0.wireOp",EDGE,"E44"),sQuery(id+"F0.wireOp",EDGE,"E45"),sQuery(id+"F0.wireOp",EDGE,"E46"),sQuery(id+"F0.wireOp",EDGE,"E47"),sQuery(id+"F0.wireOp",EDGE,"E48"),sQuery(id+"F0.wireOp",EDGE,"E49"),sQuery(id+"F0.wireOp",EDGE,"E50"),sQuery(id+"F0.wireOp",EDGE,"E51"),sQuery(id+"F0.wireOp",EDGE,"E52"),sQuery(id+"F0.wireOp",EDGE,"E53"),sQuery(id+"F0.wireOp",EDGE,"E54"),sQuery(id+"F0.wireOp",EDGE,"E55"),sQuery(id+"F0.wireOp",EDGE,"E56"),sQuery(id+"F0.wireOp",EDGE,"E57"),sQuery(id+"F0.wireOp",EDGE,"E58"),sQuery(id+"F0.wireOp",EDGE,"E59"),sQuery(id+"F0.wireOp",EDGE,"E60"),sQuery(id+"F0.wireOp",EDGE,"E61"),sQuery(id+"F0.wireOp",EDGE,"E62"),sQuery(id+"F0.wireOp",EDGE,"E63"),sQuery(id+"F0.wireOp",EDGE,"E64"),sQuery(id+"F0.wireOp",EDGE,"E65"),sQuery(id+"F0.wireOp",EDGE,"E66"),sQuery(id+"F0.wireOp",EDGE,"E67"),sQuery(id+"F0.wireOp",EDGE,"E68"),sQuery(id+"F0.wireOp",EDGE,"E69"),sQuery(id+"F0.wireOp",EDGE,"E70"),sQuery(id+"F0.wireOp",EDGE,"E71"),sQuery(id+"F0.wireOp",EDGE,"E72"),sQuery(id+"F0.wireOp",EDGE,"E73"),sQuery(id+"F0.wireOp",EDGE,"E74"),sQuery(id+"F0.wireOp",EDGE,"E75"),sQuery(id+"F0.wireOp",EDGE,"E76"),sQuery(id+"F0.wireOp",EDGE,"E77"),sQuery(id+"F0.wireOp",EDGE,"E78"),sQuery(id+"F0.wireOp",EDGE,"E79"),sQuery(id+"F0.wireOp",EDGE,"E80"),sQuery(id+"F0.wireOp",EDGE,"E81"),sQuery(id+"F0.wireOp",EDGE,"E82"),sQuery(id+"F0.wireOp",EDGE,"E83"),sQuery(id+"F0.wireOp",EDGE,"E84"),sQuery(id+"F0.wireOp",EDGE,"E85"),sQuery(id+"F0.wireOp",EDGE,"E86"),sQuery(id+"F0.wireOp",EDGE,"E87"),sQuery(id+"F0.wireOp",EDGE,"E88"),sQuery(id+"F0.wireOp",EDGE,"E89"),sQuery(id+"F0.wireOp",EDGE,"E90"),sQuery(id+"F0.wireOp",EDGE,"E91"),sQuery(id+"F0.wireOp",EDGE,"E92"),sQuery(id+"F0.wireOp",EDGE,"E93"),sQuery(id+"F0.wireOp",EDGE,"E94"),sQuery(id+"F0.wireOp",EDGE,"E95"),sQuery(id+"F0.wireOp",EDGE,"E96"),sQuery(id+"F0.wireOp",EDGE,"E97"),sQuery(id+"F0.wireOp",EDGE,"E98"),sQuery(id+"F0.wireOp",EDGE,"E99"),sQuery(id+"F0.wireOp",EDGE,"E100"),sQuery(id+"F0.wireOp",EDGE,"E101"),sQuery(id+"F0.wireOp",EDGE,"E102"),sQuery(id+"F0.wireOp",EDGE,"E103"),sQuery(id+"F0.wireOp",EDGE,"E104"),sQuery(id+"F0.wireOp",EDGE,"E105"),sQuery(id+"F0.wireOp",EDGE,"E106"),sQuery(id+"F0.wireOp",EDGE,"E107"),sQuery(id+"F0.wireOp",EDGE,"E108"),sQuery(id+"F0.wireOp",EDGE,"E109"),sQuery(id+"F0.wireOp",EDGE,"E110"),sQuery(id+"F0.wireOp",EDGE,"E111"),sQuery(id+"F0.wireOp",EDGE,"E112"),sQuery(id+"F0.wireOp",EDGE,"E113"),sQuery(id+"F0.wireOp",EDGE,"E114"),sQuery(id+"F0.wireOp",EDGE,"E115"),sQuery(id+"F0.wireOp",EDGE,"E116"),sQuery(id+"F0.wireOp",EDGE,"E117"),sQuery(id+"F0.wireOp",EDGE,"E118"),sQuery(id+"F0.wireOp",EDGE,"E119"),sQuery(id+"F0.wireOp",EDGE,"E120"),sQuery(id+"F0.wireOp",EDGE,"E121"),sQuery(id+"F0.wireOp",EDGE,"E122"),sQuery(id+"F0.wireOp",EDGE,"E123"),sQuery(id+"F0.wireOp",EDGE,"E124"),sQuery(id+"F0.wireOp",EDGE,"E125"),sQuery(id+"F0.wireOp",EDGE,"E126"),sQuery(id+"F0.wireOp",EDGE,"E127")])],"isStart":true}),"instanceName":"1"});
            extrude(context, id + "F10", {"entities" : qUnion([Q0]), "operationType" : NewBodyOperationType.ADD, "depth" : (320 - 1) * mm, "offsetDistance" : 25 * mm});
        }
        {
            var Q0;
            Q0=makeQuery(id+"F8.opPattern","COPY",FACE,{"derivedFrom":makeQuery(id+"F1.opExtrude","CAP_FACE",FACE,{"disambiguationData":[OSD([sQuery(id+"F0.wireOp",EDGE,"E0"),sQuery(id+"F0.wireOp",EDGE,"E1"),sQuery(id+"F0.wireOp",EDGE,"E2"),sQuery(id+"F0.wireOp",EDGE,"E3"),sQuery(id+"F0.wireOp",EDGE,"E4"),sQuery(id+"F0.wireOp",EDGE,"E5"),sQuery(id+"F0.wireOp",EDGE,"E6"),sQuery(id+"F0.wireOp",EDGE,"E7"),sQuery(id+"F0.wireOp",EDGE,"E8"),sQuery(id+"F0.wireOp",EDGE,"E9"),sQuery(id+"F0.wireOp",EDGE,"E10"),sQuery(id+"F0.wireOp",EDGE,"E11"),sQuery(id+"F0.wireOp",EDGE,"E12"),sQuery(id+"F0.wireOp",EDGE,"E13"),sQuery(id+"F0.wireOp",EDGE,"E14"),sQuery(id+"F0.wireOp",EDGE,"E15"),sQuery(id+"F0.wireOp",EDGE,"E16"),sQuery(id+"F0.wireOp",EDGE,"E17"),sQuery(id+"F0.wireOp",EDGE,"E18"),sQuery(id+"F0.wireOp",EDGE,"E19"),sQuery(id+"F0.wireOp",EDGE,"E20"),sQuery(id+"F0.wireOp",EDGE,"E21"),sQuery(id+"F0.wireOp",EDGE,"E22"),sQuery(id+"F0.wireOp",EDGE,"E23"),sQuery(id+"F0.wireOp",EDGE,"E24"),sQuery(id+"F0.wireOp",EDGE,"E25"),sQuery(id+"F0.wireOp",EDGE,"E26"),sQuery(id+"F0.wireOp",EDGE,"E27"),sQuery(id+"F0.wireOp",EDGE,"E28"),sQuery(id+"F0.wireOp",EDGE,"E29"),sQuery(id+"F0.wireOp",EDGE,"E30"),sQuery(id+"F0.wireOp",EDGE,"E31"),sQuery(id+"F0.wireOp",EDGE,"E32"),sQuery(id+"F0.wireOp",EDGE,"E33"),sQuery(id+"F0.wireOp",EDGE,"E34"),sQuery(id+"F0.wireOp",EDGE,"E35"),sQuery(id+"F0.wireOp",EDGE,"E36"),sQuery(id+"F0.wireOp",EDGE,"E37"),sQuery(id+"F0.wireOp",EDGE,"E38"),sQuery(id+"F0.wireOp",EDGE,"E39"),sQuery(id+"F0.wireOp",EDGE,"E40"),sQuery(id+"F0.wireOp",EDGE,"E41"),sQuery(id+"F0.wireOp",EDGE,"E42"),sQuery(id+"F0.wireOp",EDGE,"E43"),sQuery(id+"F0.wireOp",EDGE,"E44"),sQuery(id+"F0.wireOp",EDGE,"E45"),sQuery(id+"F0.wireOp",EDGE,"E46"),sQuery(id+"F0.wireOp",EDGE,"E47"),sQuery(id+"F0.wireOp",EDGE,"E48"),sQuery(id+"F0.wireOp",EDGE,"E49"),sQuery(id+"F0.wireOp",EDGE,"E50"),sQuery(id+"F0.wireOp",EDGE,"E51"),sQuery(id+"F0.wireOp",EDGE,"E52"),sQuery(id+"F0.wireOp",EDGE,"E53"),sQuery(id+"F0.wireOp",EDGE,"E54"),sQuery(id+"F0.wireOp",EDGE,"E55"),sQuery(id+"F0.wireOp",EDGE,"E56"),sQuery(id+"F0.wireOp",EDGE,"E57"),sQuery(id+"F0.wireOp",EDGE,"E58"),sQuery(id+"F0.wireOp",EDGE,"E59"),sQuery(id+"F0.wireOp",EDGE,"E60"),sQuery(id+"F0.wireOp",EDGE,"E61"),sQuery(id+"F0.wireOp",EDGE,"E62"),sQuery(id+"F0.wireOp",EDGE,"E63"),sQuery(id+"F0.wireOp",EDGE,"E64"),sQuery(id+"F0.wireOp",EDGE,"E65"),sQuery(id+"F0.wireOp",EDGE,"E66"),sQuery(id+"F0.wireOp",EDGE,"E67"),sQuery(id+"F0.wireOp",EDGE,"E68"),sQuery(id+"F0.wireOp",EDGE,"E69"),sQuery(id+"F0.wireOp",EDGE,"E70"),sQuery(id+"F0.wireOp",EDGE,"E71"),sQuery(id+"F0.wireOp",EDGE,"E72"),sQuery(id+"F0.wireOp",EDGE,"E73"),sQuery(id+"F0.wireOp",EDGE,"E74"),sQuery(id+"F0.wireOp",EDGE,"E75"),sQuery(id+"F0.wireOp",EDGE,"E76"),sQuery(id+"F0.wireOp",EDGE,"E77"),sQuery(id+"F0.wireOp",EDGE,"E78"),sQuery(id+"F0.wireOp",EDGE,"E79"),sQuery(id+"F0.wireOp",EDGE,"E80"),sQuery(id+"F0.wireOp",EDGE,"E81"),sQuery(id+"F0.wireOp",EDGE,"E82"),sQuery(id+"F0.wireOp",EDGE,"E83"),sQuery(id+"F0.wireOp",EDGE,"E84"),sQuery(id+"F0.wireOp",EDGE,"E85"),sQuery(id+"F0.wireOp",EDGE,"E86"),sQuery(id+"F0.wireOp",EDGE,"E87"),sQuery(id+"F0.wireOp",EDGE,"E88"),sQuery(id+"F0.wireOp",EDGE,"E89"),sQuery(id+"F0.wireOp",EDGE,"E90"),sQuery(id+"F0.wireOp",EDGE,"E91"),sQuery(id+"F0.wireOp",EDGE,"E92"),sQuery(id+"F0.wireOp",EDGE,"E93"),sQuery(id+"F0.wireOp",EDGE,"E94"),sQuery(id+"F0.wireOp",EDGE,"E95"),sQuery(id+"F0.wireOp",EDGE,"E96"),sQuery(id+"F0.wireOp",EDGE,"E97"),sQuery(id+"F0.wireOp",EDGE,"E98"),sQuery(id+"F0.wireOp",EDGE,"E99"),sQuery(id+"F0.wireOp",EDGE,"E100"),sQuery(id+"F0.wireOp",EDGE,"E101"),sQuery(id+"F0.wireOp",EDGE,"E102"),sQuery(id+"F0.wireOp",EDGE,"E103"),sQuery(id+"F0.wireOp",EDGE,"E104"),sQuery(id+"F0.wireOp",EDGE,"E105"),sQuery(id+"F0.wireOp",EDGE,"E106"),sQuery(id+"F0.wireOp",EDGE,"E107"),sQuery(id+"F0.wireOp",EDGE,"E108"),sQuery(id+"F0.wireOp",EDGE,"E109"),sQuery(id+"F0.wireOp",EDGE,"E110"),sQuery(id+"F0.wireOp",EDGE,"E111"),sQuery(id+"F0.wireOp",EDGE,"E112"),sQuery(id+"F0.wireOp",EDGE,"E113"),sQuery(id+"F0.wireOp",EDGE,"E114"),sQuery(id+"F0.wireOp",EDGE,"E115"),sQuery(id+"F0.wireOp",EDGE,"E116"),sQuery(id+"F0.wireOp",EDGE,"E117"),sQuery(id+"F0.wireOp",EDGE,"E118"),sQuery(id+"F0.wireOp",EDGE,"E119"),sQuery(id+"F0.wireOp",EDGE,"E120"),sQuery(id+"F0.wireOp",EDGE,"E121"),sQuery(id+"F0.wireOp",EDGE,"E122"),sQuery(id+"F0.wireOp",EDGE,"E123"),sQuery(id+"F0.wireOp",EDGE,"E124"),sQuery(id+"F0.wireOp",EDGE,"E125"),sQuery(id+"F0.wireOp",EDGE,"E126"),sQuery(id+"F0.wireOp",EDGE,"E127")])],"isStart":true}),"instanceName":"1"});
            extrude(context, id + "F11", {"entities" : qUnion([Q0]), "operationType" : NewBodyOperationType.ADD, "depth" : (159 - 1) * mm, "offsetDistance" : 25 * mm});
        }
        {
            var Q0;
            Q0=makeQuery(id+"F1.opExtrude","SWEPT_BODY",BODY,{"disambiguationData":[OSD([sQuery(id+"F0.wireOp",EDGE,"E0"),sQuery(id+"F0.wireOp",EDGE,"E1"),sQuery(id+"F0.wireOp",EDGE,"E2"),sQuery(id+"F0.wireOp",EDGE,"E3"),sQuery(id+"F0.wireOp",EDGE,"E4"),sQuery(id+"F0.wireOp",EDGE,"E5"),sQuery(id+"F0.wireOp",EDGE,"E6"),sQuery(id+"F0.wireOp",EDGE,"E7"),sQuery(id+"F0.wireOp",EDGE,"E8"),sQuery(id+"F0.wireOp",EDGE,"E9"),sQuery(id+"F0.wireOp",EDGE,"E10"),sQuery(id+"F0.wireOp",EDGE,"E11"),sQuery(id+"F0.wireOp",EDGE,"E12"),sQuery(id+"F0.wireOp",EDGE,"E13"),sQuery(id+"F0.wireOp",EDGE,"E14"),sQuery(id+"F0.wireOp",EDGE,"E15"),sQuery(id+"F0.wireOp",EDGE,"E16"),sQuery(id+"F0.wireOp",EDGE,"E17"),sQuery(id+"F0.wireOp",EDGE,"E18"),sQuery(id+"F0.wireOp",EDGE,"E19"),sQuery(id+"F0.wireOp",EDGE,"E20"),sQuery(id+"F0.wireOp",EDGE,"E21"),sQuery(id+"F0.wireOp",EDGE,"E22"),sQuery(id+"F0.wireOp",EDGE,"E23"),sQuery(id+"F0.wireOp",EDGE,"E24"),sQuery(id+"F0.wireOp",EDGE,"E25"),sQuery(id+"F0.wireOp",EDGE,"E26"),sQuery(id+"F0.wireOp",EDGE,"E27"),sQuery(id+"F0.wireOp",EDGE,"E28"),sQuery(id+"F0.wireOp",EDGE,"E29"),sQuery(id+"F0.wireOp",EDGE,"E30"),sQuery(id+"F0.wireOp",EDGE,"E31"),sQuery(id+"F0.wireOp",EDGE,"E32"),sQuery(id+"F0.wireOp",EDGE,"E33"),sQuery(id+"F0.wireOp",EDGE,"E34"),sQuery(id+"F0.wireOp",EDGE,"E35"),sQuery(id+"F0.wireOp",EDGE,"E36"),sQuery(id+"F0.wireOp",EDGE,"E37"),sQuery(id+"F0.wireOp",EDGE,"E38"),sQuery(id+"F0.wireOp",EDGE,"E39"),sQuery(id+"F0.wireOp",EDGE,"E40"),sQuery(id+"F0.wireOp",EDGE,"E41"),sQuery(id+"F0.wireOp",EDGE,"E42"),sQuery(id+"F0.wireOp",EDGE,"E43"),sQuery(id+"F0.wireOp",EDGE,"E44"),sQuery(id+"F0.wireOp",EDGE,"E45"),sQuery(id+"F0.wireOp",EDGE,"E46"),sQuery(id+"F0.wireOp",EDGE,"E47"),sQuery(id+"F0.wireOp",EDGE,"E48"),sQuery(id+"F0.wireOp",EDGE,"E49"),sQuery(id+"F0.wireOp",EDGE,"E50"),sQuery(id+"F0.wireOp",EDGE,"E51"),sQuery(id+"F0.wireOp",EDGE,"E52"),sQuery(id+"F0.wireOp",EDGE,"E53"),sQuery(id+"F0.wireOp",EDGE,"E54"),sQuery(id+"F0.wireOp",EDGE,"E55"),sQuery(id+"F0.wireOp",EDGE,"E56"),sQuery(id+"F0.wireOp",EDGE,"E57"),sQuery(id+"F0.wireOp",EDGE,"E58"),sQuery(id+"F0.wireOp",EDGE,"E59"),sQuery(id+"F0.wireOp",EDGE,"E60"),sQuery(id+"F0.wireOp",EDGE,"E61"),sQuery(id+"F0.wireOp",EDGE,"E62"),sQuery(id+"F0.wireOp",EDGE,"E63"),sQuery(id+"F0.wireOp",EDGE,"E64"),sQuery(id+"F0.wireOp",EDGE,"E65"),sQuery(id+"F0.wireOp",EDGE,"E66"),sQuery(id+"F0.wireOp",EDGE,"E67"),sQuery(id+"F0.wireOp",EDGE,"E68"),sQuery(id+"F0.wireOp",EDGE,"E69"),sQuery(id+"F0.wireOp",EDGE,"E70"),sQuery(id+"F0.wireOp",EDGE,"E71"),sQuery(id+"F0.wireOp",EDGE,"E72"),sQuery(id+"F0.wireOp",EDGE,"E73"),sQuery(id+"F0.wireOp",EDGE,"E74"),sQuery(id+"F0.wireOp",EDGE,"E75"),sQuery(id+"F0.wireOp",EDGE,"E76"),sQuery(id+"F0.wireOp",EDGE,"E77"),sQuery(id+"F0.wireOp",EDGE,"E78"),sQuery(id+"F0.wireOp",EDGE,"E79"),sQuery(id+"F0.wireOp",EDGE,"E80"),sQuery(id+"F0.wireOp",EDGE,"E81"),sQuery(id+"F0.wireOp",EDGE,"E82"),sQuery(id+"F0.wireOp",EDGE,"E83"),sQuery(id+"F0.wireOp",EDGE,"E84"),sQuery(id+"F0.wireOp",EDGE,"E85"),sQuery(id+"F0.wireOp",EDGE,"E86"),sQuery(id+"F0.wireOp",EDGE,"E87"),sQuery(id+"F0.wireOp",EDGE,"E88"),sQuery(id+"F0.wireOp",EDGE,"E89"),sQuery(id+"F0.wireOp",EDGE,"E90"),sQuery(id+"F0.wireOp",EDGE,"E91"),sQuery(id+"F0.wireOp",EDGE,"E92"),sQuery(id+"F0.wireOp",EDGE,"E93"),sQuery(id+"F0.wireOp",EDGE,"E94"),sQuery(id+"F0.wireOp",EDGE,"E95"),sQuery(id+"F0.wireOp",EDGE,"E96"),sQuery(id+"F0.wireOp",EDGE,"E97"),sQuery(id+"F0.wireOp",EDGE,"E98"),sQuery(id+"F0.wireOp",EDGE,"E99"),sQuery(id+"F0.wireOp",EDGE,"E100"),sQuery(id+"F0.wireOp",EDGE,"E101"),sQuery(id+"F0.wireOp",EDGE,"E102"),sQuery(id+"F0.wireOp",EDGE,"E103"),sQuery(id+"F0.wireOp",EDGE,"E104"),sQuery(id+"F0.wireOp",EDGE,"E105"),sQuery(id+"F0.wireOp",EDGE,"E106"),sQuery(id+"F0.wireOp",EDGE,"E107"),sQuery(id+"F0.wireOp",EDGE,"E108"),sQuery(id+"F0.wireOp",EDGE,"E109"),sQuery(id+"F0.wireOp",EDGE,"E110"),sQuery(id+"F0.wireOp",EDGE,"E111"),sQuery(id+"F0.wireOp",EDGE,"E112"),sQuery(id+"F0.wireOp",EDGE,"E113"),sQuery(id+"F0.wireOp",EDGE,"E114"),sQuery(id+"F0.wireOp",EDGE,"E115"),sQuery(id+"F0.wireOp",EDGE,"E116"),sQuery(id+"F0.wireOp",EDGE,"E117"),sQuery(id+"F0.wireOp",EDGE,"E118"),sQuery(id+"F0.wireOp",EDGE,"E119"),sQuery(id+"F0.wireOp",EDGE,"E120"),sQuery(id+"F0.wireOp",EDGE,"E121"),sQuery(id+"F0.wireOp",EDGE,"E122"),sQuery(id+"F0.wireOp",EDGE,"E123"),sQuery(id+"F0.wireOp",EDGE,"E124"),sQuery(id+"F0.wireOp",EDGE,"E125"),sQuery(id+"F0.wireOp",EDGE,"E126"),sQuery(id+"F0.wireOp",EDGE,"E127")])]});
            transform(context, id + "F12", {"entities" : qUnion([Q0]), "transformType" : TransformType.TRANSLATION_3D, "dx" : (25 * 6) * mm, "dy" : 0 * mm, "dz" : 0 * mm, "makeCopy" : true});
        }
        {
            var Q0;
            Q0=makeQuery(id+"F1.opExtrude","SWEPT_BODY",BODY,{"disambiguationData":[OSD([sQuery(id+"F0.wireOp",EDGE,"E0"),sQuery(id+"F0.wireOp",EDGE,"E1"),sQuery(id+"F0.wireOp",EDGE,"E2"),sQuery(id+"F0.wireOp",EDGE,"E3"),sQuery(id+"F0.wireOp",EDGE,"E4"),sQuery(id+"F0.wireOp",EDGE,"E5"),sQuery(id+"F0.wireOp",EDGE,"E6"),sQuery(id+"F0.wireOp",EDGE,"E7"),sQuery(id+"F0.wireOp",EDGE,"E8"),sQuery(id+"F0.wireOp",EDGE,"E9"),sQuery(id+"F0.wireOp",EDGE,"E10"),sQuery(id+"F0.wireOp",EDGE,"E11"),sQuery(id+"F0.wireOp",EDGE,"E12"),sQuery(id+"F0.wireOp",EDGE,"E13"),sQuery(id+"F0.wireOp",EDGE,"E14"),sQuery(id+"F0.wireOp",EDGE,"E15"),sQuery(id+"F0.wireOp",EDGE,"E16"),sQuery(id+"F0.wireOp",EDGE,"E17"),sQuery(id+"F0.wireOp",EDGE,"E18"),sQuery(id+"F0.wireOp",EDGE,"E19"),sQuery(id+"F0.wireOp",EDGE,"E20"),sQuery(id+"F0.wireOp",EDGE,"E21"),sQuery(id+"F0.wireOp",EDGE,"E22"),sQuery(id+"F0.wireOp",EDGE,"E23"),sQuery(id+"F0.wireOp",EDGE,"E24"),sQuery(id+"F0.wireOp",EDGE,"E25"),sQuery(id+"F0.wireOp",EDGE,"E26"),sQuery(id+"F0.wireOp",EDGE,"E27"),sQuery(id+"F0.wireOp",EDGE,"E28"),sQuery(id+"F0.wireOp",EDGE,"E29"),sQuery(id+"F0.wireOp",EDGE,"E30"),sQuery(id+"F0.wireOp",EDGE,"E31"),sQuery(id+"F0.wireOp",EDGE,"E32"),sQuery(id+"F0.wireOp",EDGE,"E33"),sQuery(id+"F0.wireOp",EDGE,"E34"),sQuery(id+"F0.wireOp",EDGE,"E35"),sQuery(id+"F0.wireOp",EDGE,"E36"),sQuery(id+"F0.wireOp",EDGE,"E37"),sQuery(id+"F0.wireOp",EDGE,"E38"),sQuery(id+"F0.wireOp",EDGE,"E39"),sQuery(id+"F0.wireOp",EDGE,"E40"),sQuery(id+"F0.wireOp",EDGE,"E41"),sQuery(id+"F0.wireOp",EDGE,"E42"),sQuery(id+"F0.wireOp",EDGE,"E43"),sQuery(id+"F0.wireOp",EDGE,"E44"),sQuery(id+"F0.wireOp",EDGE,"E45"),sQuery(id+"F0.wireOp",EDGE,"E46"),sQuery(id+"F0.wireOp",EDGE,"E47"),sQuery(id+"F0.wireOp",EDGE,"E48"),sQuery(id+"F0.wireOp",EDGE,"E49"),sQuery(id+"F0.wireOp",EDGE,"E50"),sQuery(id+"F0.wireOp",EDGE,"E51"),sQuery(id+"F0.wireOp",EDGE,"E52"),sQuery(id+"F0.wireOp",EDGE,"E53"),sQuery(id+"F0.wireOp",EDGE,"E54"),sQuery(id+"F0.wireOp",EDGE,"E55"),sQuery(id+"F0.wireOp",EDGE,"E56"),sQuery(id+"F0.wireOp",EDGE,"E57"),sQuery(id+"F0.wireOp",EDGE,"E58"),sQuery(id+"F0.wireOp",EDGE,"E59"),sQuery(id+"F0.wireOp",EDGE,"E60"),sQuery(id+"F0.wireOp",EDGE,"E61"),sQuery(id+"F0.wireOp",EDGE,"E62"),sQuery(id+"F0.wireOp",EDGE,"E63"),sQuery(id+"F0.wireOp",EDGE,"E64"),sQuery(id+"F0.wireOp",EDGE,"E65"),sQuery(id+"F0.wireOp",EDGE,"E66"),sQuery(id+"F0.wireOp",EDGE,"E67"),sQuery(id+"F0.wireOp",EDGE,"E68"),sQuery(id+"F0.wireOp",EDGE,"E69"),sQuery(id+"F0.wireOp",EDGE,"E70"),sQuery(id+"F0.wireOp",EDGE,"E71"),sQuery(id+"F0.wireOp",EDGE,"E72"),sQuery(id+"F0.wireOp",EDGE,"E73"),sQuery(id+"F0.wireOp",EDGE,"E74"),sQuery(id+"F0.wireOp",EDGE,"E75"),sQuery(id+"F0.wireOp",EDGE,"E76"),sQuery(id+"F0.wireOp",EDGE,"E77"),sQuery(id+"F0.wireOp",EDGE,"E78"),sQuery(id+"F0.wireOp",EDGE,"E79"),sQuery(id+"F0.wireOp",EDGE,"E80"),sQuery(id+"F0.wireOp",EDGE,"E81"),sQuery(id+"F0.wireOp",EDGE,"E82"),sQuery(id+"F0.wireOp",EDGE,"E83"),sQuery(id+"F0.wireOp",EDGE,"E84"),sQuery(id+"F0.wireOp",EDGE,"E85"),sQuery(id+"F0.wireOp",EDGE,"E86"),sQuery(id+"F0.wireOp",EDGE,"E87"),sQuery(id+"F0.wireOp",EDGE,"E88"),sQuery(id+"F0.wireOp",EDGE,"E89"),sQuery(id+"F0.wireOp",EDGE,"E90"),sQuery(id+"F0.wireOp",EDGE,"E91"),sQuery(id+"F0.wireOp",EDGE,"E92"),sQuery(id+"F0.wireOp",EDGE,"E93"),sQuery(id+"F0.wireOp",EDGE,"E94"),sQuery(id+"F0.wireOp",EDGE,"E95"),sQuery(id+"F0.wireOp",EDGE,"E96"),sQuery(id+"F0.wireOp",EDGE,"E97"),sQuery(id+"F0.wireOp",EDGE,"E98"),sQuery(id+"F0.wireOp",EDGE,"E99"),sQuery(id+"F0.wireOp",EDGE,"E100"),sQuery(id+"F0.wireOp",EDGE,"E101"),sQuery(id+"F0.wireOp",EDGE,"E102"),sQuery(id+"F0.wireOp",EDGE,"E103"),sQuery(id+"F0.wireOp",EDGE,"E104"),sQuery(id+"F0.wireOp",EDGE,"E105"),sQuery(id+"F0.wireOp",EDGE,"E106"),sQuery(id+"F0.wireOp",EDGE,"E107"),sQuery(id+"F0.wireOp",EDGE,"E108"),sQuery(id+"F0.wireOp",EDGE,"E109"),sQuery(id+"F0.wireOp",EDGE,"E110"),sQuery(id+"F0.wireOp",EDGE,"E111"),sQuery(id+"F0.wireOp",EDGE,"E112"),sQuery(id+"F0.wireOp",EDGE,"E113"),sQuery(id+"F0.wireOp",EDGE,"E114"),sQuery(id+"F0.wireOp",EDGE,"E115"),sQuery(id+"F0.wireOp",EDGE,"E116"),sQuery(id+"F0.wireOp",EDGE,"E117"),sQuery(id+"F0.wireOp",EDGE,"E118"),sQuery(id+"F0.wireOp",EDGE,"E119"),sQuery(id+"F0.wireOp",EDGE,"E120"),sQuery(id+"F0.wireOp",EDGE,"E121"),sQuery(id+"F0.wireOp",EDGE,"E122"),sQuery(id+"F0.wireOp",EDGE,"E123"),sQuery(id+"F0.wireOp",EDGE,"E124"),sQuery(id+"F0.wireOp",EDGE,"E125"),sQuery(id+"F0.wireOp",EDGE,"E126"),sQuery(id+"F0.wireOp",EDGE,"E127")])]});
            transform(context, id + "F13", {"entities" : qUnion([Q0]), "transformType" : TransformType.TRANSLATION_3D, "dx" : (25 * 7) * mm, "dy" : 0 * mm, "dz" : 0 * mm, "makeCopy" : true});
        }
        {
            var Q0;
            Q0=makeQuery(id+"F12.opPattern","COPY",FACE,{"derivedFrom":makeQuery(id+"F1.opExtrude","CAP_FACE",FACE,{"disambiguationData":[OSD([sQuery(id+"F0.wireOp",EDGE,"E0"),sQuery(id+"F0.wireOp",EDGE,"E1"),sQuery(id+"F0.wireOp",EDGE,"E2"),sQuery(id+"F0.wireOp",EDGE,"E3"),sQuery(id+"F0.wireOp",EDGE,"E4"),sQuery(id+"F0.wireOp",EDGE,"E5"),sQuery(id+"F0.wireOp",EDGE,"E6"),sQuery(id+"F0.wireOp",EDGE,"E7"),sQuery(id+"F0.wireOp",EDGE,"E8"),sQuery(id+"F0.wireOp",EDGE,"E9"),sQuery(id+"F0.wireOp",EDGE,"E10"),sQuery(id+"F0.wireOp",EDGE,"E11"),sQuery(id+"F0.wireOp",EDGE,"E12"),sQuery(id+"F0.wireOp",EDGE,"E13"),sQuery(id+"F0.wireOp",EDGE,"E14"),sQuery(id+"F0.wireOp",EDGE,"E15"),sQuery(id+"F0.wireOp",EDGE,"E16"),sQuery(id+"F0.wireOp",EDGE,"E17"),sQuery(id+"F0.wireOp",EDGE,"E18"),sQuery(id+"F0.wireOp",EDGE,"E19"),sQuery(id+"F0.wireOp",EDGE,"E20"),sQuery(id+"F0.wireOp",EDGE,"E21"),sQuery(id+"F0.wireOp",EDGE,"E22"),sQuery(id+"F0.wireOp",EDGE,"E23"),sQuery(id+"F0.wireOp",EDGE,"E24"),sQuery(id+"F0.wireOp",EDGE,"E25"),sQuery(id+"F0.wireOp",EDGE,"E26"),sQuery(id+"F0.wireOp",EDGE,"E27"),sQuery(id+"F0.wireOp",EDGE,"E28"),sQuery(id+"F0.wireOp",EDGE,"E29"),sQuery(id+"F0.wireOp",EDGE,"E30"),sQuery(id+"F0.wireOp",EDGE,"E31"),sQuery(id+"F0.wireOp",EDGE,"E32"),sQuery(id+"F0.wireOp",EDGE,"E33"),sQuery(id+"F0.wireOp",EDGE,"E34"),sQuery(id+"F0.wireOp",EDGE,"E35"),sQuery(id+"F0.wireOp",EDGE,"E36"),sQuery(id+"F0.wireOp",EDGE,"E37"),sQuery(id+"F0.wireOp",EDGE,"E38"),sQuery(id+"F0.wireOp",EDGE,"E39"),sQuery(id+"F0.wireOp",EDGE,"E40"),sQuery(id+"F0.wireOp",EDGE,"E41"),sQuery(id+"F0.wireOp",EDGE,"E42"),sQuery(id+"F0.wireOp",EDGE,"E43"),sQuery(id+"F0.wireOp",EDGE,"E44"),sQuery(id+"F0.wireOp",EDGE,"E45"),sQuery(id+"F0.wireOp",EDGE,"E46"),sQuery(id+"F0.wireOp",EDGE,"E47"),sQuery(id+"F0.wireOp",EDGE,"E48"),sQuery(id+"F0.wireOp",EDGE,"E49"),sQuery(id+"F0.wireOp",EDGE,"E50"),sQuery(id+"F0.wireOp",EDGE,"E51"),sQuery(id+"F0.wireOp",EDGE,"E52"),sQuery(id+"F0.wireOp",EDGE,"E53"),sQuery(id+"F0.wireOp",EDGE,"E54"),sQuery(id+"F0.wireOp",EDGE,"E55"),sQuery(id+"F0.wireOp",EDGE,"E56"),sQuery(id+"F0.wireOp",EDGE,"E57"),sQuery(id+"F0.wireOp",EDGE,"E58"),sQuery(id+"F0.wireOp",EDGE,"E59"),sQuery(id+"F0.wireOp",EDGE,"E60"),sQuery(id+"F0.wireOp",EDGE,"E61"),sQuery(id+"F0.wireOp",EDGE,"E62"),sQuery(id+"F0.wireOp",EDGE,"E63"),sQuery(id+"F0.wireOp",EDGE,"E64"),sQuery(id+"F0.wireOp",EDGE,"E65"),sQuery(id+"F0.wireOp",EDGE,"E66"),sQuery(id+"F0.wireOp",EDGE,"E67"),sQuery(id+"F0.wireOp",EDGE,"E68"),sQuery(id+"F0.wireOp",EDGE,"E69"),sQuery(id+"F0.wireOp",EDGE,"E70"),sQuery(id+"F0.wireOp",EDGE,"E71"),sQuery(id+"F0.wireOp",EDGE,"E72"),sQuery(id+"F0.wireOp",EDGE,"E73"),sQuery(id+"F0.wireOp",EDGE,"E74"),sQuery(id+"F0.wireOp",EDGE,"E75"),sQuery(id+"F0.wireOp",EDGE,"E76"),sQuery(id+"F0.wireOp",EDGE,"E77"),sQuery(id+"F0.wireOp",EDGE,"E78"),sQuery(id+"F0.wireOp",EDGE,"E79"),sQuery(id+"F0.wireOp",EDGE,"E80"),sQuery(id+"F0.wireOp",EDGE,"E81"),sQuery(id+"F0.wireOp",EDGE,"E82"),sQuery(id+"F0.wireOp",EDGE,"E83"),sQuery(id+"F0.wireOp",EDGE,"E84"),sQuery(id+"F0.wireOp",EDGE,"E85"),sQuery(id+"F0.wireOp",EDGE,"E86"),sQuery(id+"F0.wireOp",EDGE,"E87"),sQuery(id+"F0.wireOp",EDGE,"E88"),sQuery(id+"F0.wireOp",EDGE,"E89"),sQuery(id+"F0.wireOp",EDGE,"E90"),sQuery(id+"F0.wireOp",EDGE,"E91"),sQuery(id+"F0.wireOp",EDGE,"E92"),sQuery(id+"F0.wireOp",EDGE,"E93"),sQuery(id+"F0.wireOp",EDGE,"E94"),sQuery(id+"F0.wireOp",EDGE,"E95"),sQuery(id+"F0.wireOp",EDGE,"E96"),sQuery(id+"F0.wireOp",EDGE,"E97"),sQuery(id+"F0.wireOp",EDGE,"E98"),sQuery(id+"F0.wireOp",EDGE,"E99"),sQuery(id+"F0.wireOp",EDGE,"E100"),sQuery(id+"F0.wireOp",EDGE,"E101"),sQuery(id+"F0.wireOp",EDGE,"E102"),sQuery(id+"F0.wireOp",EDGE,"E103"),sQuery(id+"F0.wireOp",EDGE,"E104"),sQuery(id+"F0.wireOp",EDGE,"E105"),sQuery(id+"F0.wireOp",EDGE,"E106"),sQuery(id+"F0.wireOp",EDGE,"E107"),sQuery(id+"F0.wireOp",EDGE,"E108"),sQuery(id+"F0.wireOp",EDGE,"E109"),sQuery(id+"F0.wireOp",EDGE,"E110"),sQuery(id+"F0.wireOp",EDGE,"E111"),sQuery(id+"F0.wireOp",EDGE,"E112"),sQuery(id+"F0.wireOp",EDGE,"E113"),sQuery(id+"F0.wireOp",EDGE,"E114"),sQuery(id+"F0.wireOp",EDGE,"E115"),sQuery(id+"F0.wireOp",EDGE,"E116"),sQuery(id+"F0.wireOp",EDGE,"E117"),sQuery(id+"F0.wireOp",EDGE,"E118"),sQuery(id+"F0.wireOp",EDGE,"E119"),sQuery(id+"F0.wireOp",EDGE,"E120"),sQuery(id+"F0.wireOp",EDGE,"E121"),sQuery(id+"F0.wireOp",EDGE,"E122"),sQuery(id+"F0.wireOp",EDGE,"E123"),sQuery(id+"F0.wireOp",EDGE,"E124"),sQuery(id+"F0.wireOp",EDGE,"E125"),sQuery(id+"F0.wireOp",EDGE,"E126"),sQuery(id+"F0.wireOp",EDGE,"E127")])],"isStart":true}),"instanceName":"1"});
            extrude(context, id + "F14", {"entities" : qUnion([Q0]), "operationType" : NewBodyOperationType.ADD, "depth" : (480 - 1) * mm, "offsetDistance" : 25 * mm});
        }
        {
            var Q0;
            Q0=makeQuery(id+"F13.opPattern","COPY",FACE,{"derivedFrom":makeQuery(id+"F1.opExtrude","CAP_FACE",FACE,{"disambiguationData":[OSD([sQuery(id+"F0.wireOp",EDGE,"E0"),sQuery(id+"F0.wireOp",EDGE,"E1"),sQuery(id+"F0.wireOp",EDGE,"E2"),sQuery(id+"F0.wireOp",EDGE,"E3"),sQuery(id+"F0.wireOp",EDGE,"E4"),sQuery(id+"F0.wireOp",EDGE,"E5"),sQuery(id+"F0.wireOp",EDGE,"E6"),sQuery(id+"F0.wireOp",EDGE,"E7"),sQuery(id+"F0.wireOp",EDGE,"E8"),sQuery(id+"F0.wireOp",EDGE,"E9"),sQuery(id+"F0.wireOp",EDGE,"E10"),sQuery(id+"F0.wireOp",EDGE,"E11"),sQuery(id+"F0.wireOp",EDGE,"E12"),sQuery(id+"F0.wireOp",EDGE,"E13"),sQuery(id+"F0.wireOp",EDGE,"E14"),sQuery(id+"F0.wireOp",EDGE,"E15"),sQuery(id+"F0.wireOp",EDGE,"E16"),sQuery(id+"F0.wireOp",EDGE,"E17"),sQuery(id+"F0.wireOp",EDGE,"E18"),sQuery(id+"F0.wireOp",EDGE,"E19"),sQuery(id+"F0.wireOp",EDGE,"E20"),sQuery(id+"F0.wireOp",EDGE,"E21"),sQuery(id+"F0.wireOp",EDGE,"E22"),sQuery(id+"F0.wireOp",EDGE,"E23"),sQuery(id+"F0.wireOp",EDGE,"E24"),sQuery(id+"F0.wireOp",EDGE,"E25"),sQuery(id+"F0.wireOp",EDGE,"E26"),sQuery(id+"F0.wireOp",EDGE,"E27"),sQuery(id+"F0.wireOp",EDGE,"E28"),sQuery(id+"F0.wireOp",EDGE,"E29"),sQuery(id+"F0.wireOp",EDGE,"E30"),sQuery(id+"F0.wireOp",EDGE,"E31"),sQuery(id+"F0.wireOp",EDGE,"E32"),sQuery(id+"F0.wireOp",EDGE,"E33"),sQuery(id+"F0.wireOp",EDGE,"E34"),sQuery(id+"F0.wireOp",EDGE,"E35"),sQuery(id+"F0.wireOp",EDGE,"E36"),sQuery(id+"F0.wireOp",EDGE,"E37"),sQuery(id+"F0.wireOp",EDGE,"E38"),sQuery(id+"F0.wireOp",EDGE,"E39"),sQuery(id+"F0.wireOp",EDGE,"E40"),sQuery(id+"F0.wireOp",EDGE,"E41"),sQuery(id+"F0.wireOp",EDGE,"E42"),sQuery(id+"F0.wireOp",EDGE,"E43"),sQuery(id+"F0.wireOp",EDGE,"E44"),sQuery(id+"F0.wireOp",EDGE,"E45"),sQuery(id+"F0.wireOp",EDGE,"E46"),sQuery(id+"F0.wireOp",EDGE,"E47"),sQuery(id+"F0.wireOp",EDGE,"E48"),sQuery(id+"F0.wireOp",EDGE,"E49"),sQuery(id+"F0.wireOp",EDGE,"E50"),sQuery(id+"F0.wireOp",EDGE,"E51"),sQuery(id+"F0.wireOp",EDGE,"E52"),sQuery(id+"F0.wireOp",EDGE,"E53"),sQuery(id+"F0.wireOp",EDGE,"E54"),sQuery(id+"F0.wireOp",EDGE,"E55"),sQuery(id+"F0.wireOp",EDGE,"E56"),sQuery(id+"F0.wireOp",EDGE,"E57"),sQuery(id+"F0.wireOp",EDGE,"E58"),sQuery(id+"F0.wireOp",EDGE,"E59"),sQuery(id+"F0.wireOp",EDGE,"E60"),sQuery(id+"F0.wireOp",EDGE,"E61"),sQuery(id+"F0.wireOp",EDGE,"E62"),sQuery(id+"F0.wireOp",EDGE,"E63"),sQuery(id+"F0.wireOp",EDGE,"E64"),sQuery(id+"F0.wireOp",EDGE,"E65"),sQuery(id+"F0.wireOp",EDGE,"E66"),sQuery(id+"F0.wireOp",EDGE,"E67"),sQuery(id+"F0.wireOp",EDGE,"E68"),sQuery(id+"F0.wireOp",EDGE,"E69"),sQuery(id+"F0.wireOp",EDGE,"E70"),sQuery(id+"F0.wireOp",EDGE,"E71"),sQuery(id+"F0.wireOp",EDGE,"E72"),sQuery(id+"F0.wireOp",EDGE,"E73"),sQuery(id+"F0.wireOp",EDGE,"E74"),sQuery(id+"F0.wireOp",EDGE,"E75"),sQuery(id+"F0.wireOp",EDGE,"E76"),sQuery(id+"F0.wireOp",EDGE,"E77"),sQuery(id+"F0.wireOp",EDGE,"E78"),sQuery(id+"F0.wireOp",EDGE,"E79"),sQuery(id+"F0.wireOp",EDGE,"E80"),sQuery(id+"F0.wireOp",EDGE,"E81"),sQuery(id+"F0.wireOp",EDGE,"E82"),sQuery(id+"F0.wireOp",EDGE,"E83"),sQuery(id+"F0.wireOp",EDGE,"E84"),sQuery(id+"F0.wireOp",EDGE,"E85"),sQuery(id+"F0.wireOp",EDGE,"E86"),sQuery(id+"F0.wireOp",EDGE,"E87"),sQuery(id+"F0.wireOp",EDGE,"E88"),sQuery(id+"F0.wireOp",EDGE,"E89"),sQuery(id+"F0.wireOp",EDGE,"E90"),sQuery(id+"F0.wireOp",EDGE,"E91"),sQuery(id+"F0.wireOp",EDGE,"E92"),sQuery(id+"F0.wireOp",EDGE,"E93"),sQuery(id+"F0.wireOp",EDGE,"E94"),sQuery(id+"F0.wireOp",EDGE,"E95"),sQuery(id+"F0.wireOp",EDGE,"E96"),sQuery(id+"F0.wireOp",EDGE,"E97"),sQuery(id+"F0.wireOp",EDGE,"E98"),sQuery(id+"F0.wireOp",EDGE,"E99"),sQuery(id+"F0.wireOp",EDGE,"E100"),sQuery(id+"F0.wireOp",EDGE,"E101"),sQuery(id+"F0.wireOp",EDGE,"E102"),sQuery(id+"F0.wireOp",EDGE,"E103"),sQuery(id+"F0.wireOp",EDGE,"E104"),sQuery(id+"F0.wireOp",EDGE,"E105"),sQuery(id+"F0.wireOp",EDGE,"E106"),sQuery(id+"F0.wireOp",EDGE,"E107"),sQuery(id+"F0.wireOp",EDGE,"E108"),sQuery(id+"F0.wireOp",EDGE,"E109"),sQuery(id+"F0.wireOp",EDGE,"E110"),sQuery(id+"F0.wireOp",EDGE,"E111"),sQuery(id+"F0.wireOp",EDGE,"E112"),sQuery(id+"F0.wireOp",EDGE,"E113"),sQuery(id+"F0.wireOp",EDGE,"E114"),sQuery(id+"F0.wireOp",EDGE,"E115"),sQuery(id+"F0.wireOp",EDGE,"E116"),sQuery(id+"F0.wireOp",EDGE,"E117"),sQuery(id+"F0.wireOp",EDGE,"E118"),sQuery(id+"F0.wireOp",EDGE,"E119"),sQuery(id+"F0.wireOp",EDGE,"E120"),sQuery(id+"F0.wireOp",EDGE,"E121"),sQuery(id+"F0.wireOp",EDGE,"E122"),sQuery(id+"F0.wireOp",EDGE,"E123"),sQuery(id+"F0.wireOp",EDGE,"E124"),sQuery(id+"F0.wireOp",EDGE,"E125"),sQuery(id+"F0.wireOp",EDGE,"E126"),sQuery(id+"F0.wireOp",EDGE,"E127")])],"isStart":true}),"instanceName":"1"});
            extrude(context, id + "F15", {"entities" : qUnion([Q0]), "operationType" : NewBodyOperationType.ADD, "depth" : (650 - 1) * mm, "offsetDistance" : 25 * mm});
        }
    });
